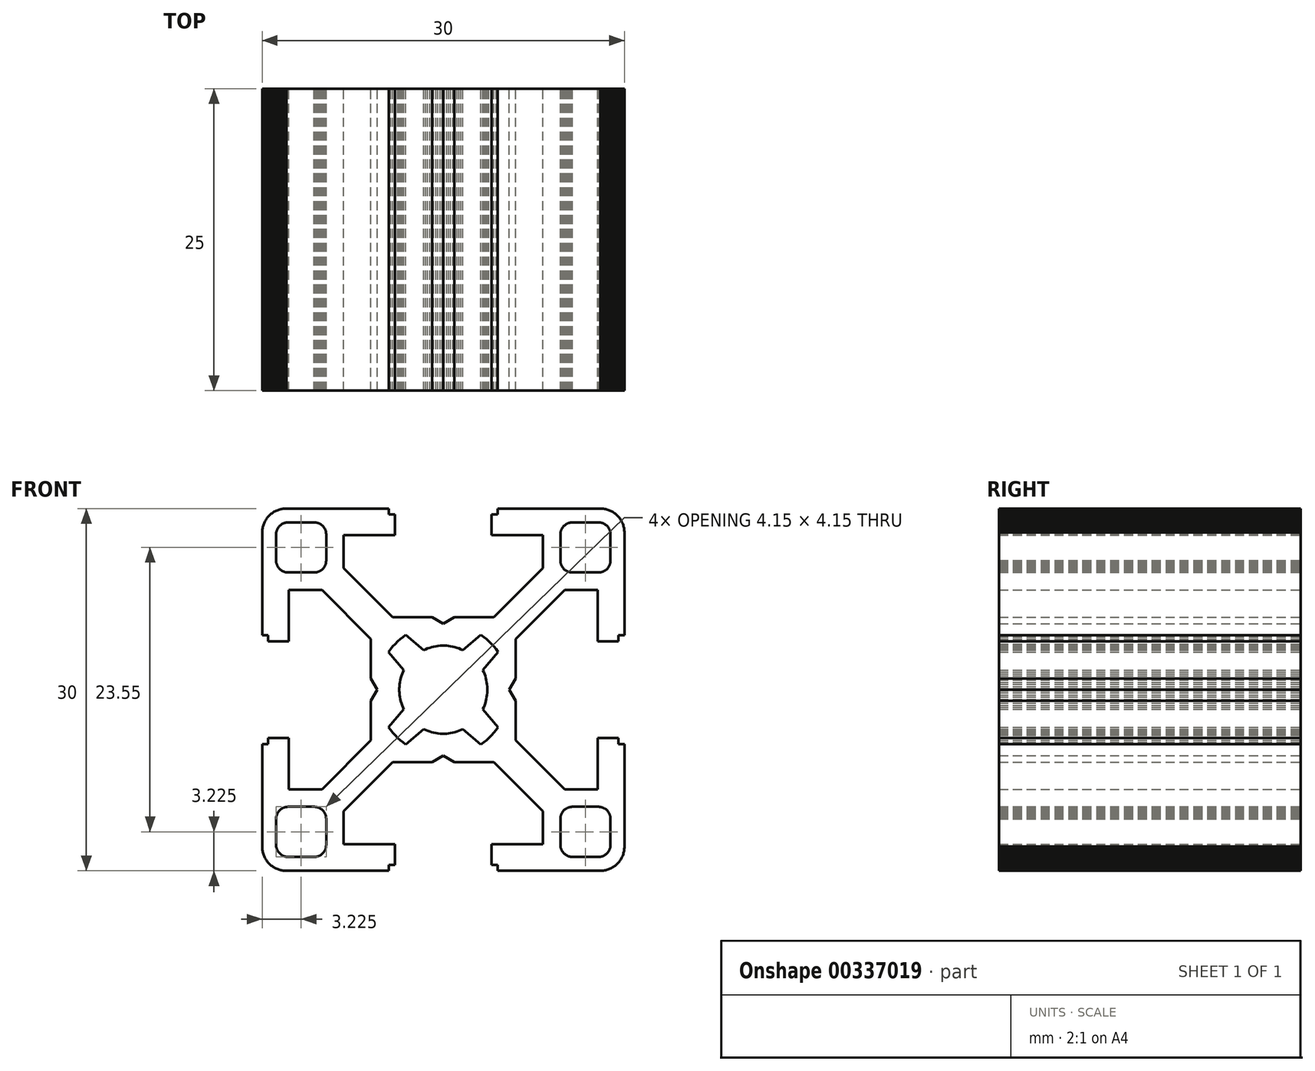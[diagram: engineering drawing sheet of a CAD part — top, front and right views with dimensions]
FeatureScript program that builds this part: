
annotation { "Feature Type Name" : "Feature", "Feature Type Description" : "" }
export const myFeature = defineFeature(function(context is Context, id is Id, definition is map)
    precondition{}
    {
        {
            var Q0;
            Q0=qCreatedBy(makeId("Front.planeOp"),FACE);
            var sketch = newSketch(context, id + "F0", { "sketchPlane" : qUnion([Q0])});
            skLineSegment(sketch, "E0", {"start": v(12.8, -8.25) * mm, "end": v(12.8, -4) * mm});
            skLineSegment(sketch, "E1", {"start": v(-12.8, 4) * mm, "end": v(-12.8, 8.25) * mm});
            skLineSegment(sketch, "E2", {"start": v(-13.85, -12.9) * mm, "end": v(-13.85, -12.85) * mm});
            skLineSegment(sketch, "E3", {"start": v(9.7, -12.9) * mm, "end": v(9.7, -12.85) * mm});
            skLineSegment(sketch, "E4", {"start": v(-9.7, -10.7) * mm, "end": v(-9.7, -10.66) * mm});
            skLineSegment(sketch, "E5", {"start": v(13.85, -10.7) * mm, "end": v(13.85, -10.66) * mm});
            skLineSegment(sketch, "E6", {"start": v(9.7, 10.66) * mm, "end": v(9.7, 10.7) * mm});
            skLineSegment(sketch, "E7", {"start": v(-13.85, 10.66) * mm, "end": v(-13.85, 10.7) * mm});
            skLineSegment(sketch, "E8", {"start": v(13.85, 12.85) * mm, "end": v(13.85, 12.9) * mm});
            skLineSegment(sketch, "E9", {"start": v(-9.7, 12.85) * mm, "end": v(-9.7, 12.9) * mm});
            skLineSegment(sketch, "E10", {"start": v(-15, -13.09) * mm, "end": v(-15, -13) * mm});
            skLineSegment(sketch, "E11", {"start": v(15, 13) * mm, "end": v(15, 13.09) * mm});
            skLineSegment(sketch, "E12", {"start": v(-3.64, -0.26) * mm, "end": v(-3.65, -0.09) * mm});
            skLineSegment(sketch, "E13", {"start": v(3.65, 0.09) * mm, "end": v(3.64, 0.26) * mm});
            skLineSegment(sketch, "E14", {"start": v(9.7, -12.94) * mm, "end": v(9.7, -12.9) * mm});
            skLineSegment(sketch, "E15", {"start": v(-9.7, -10.66) * mm, "end": v(-9.7, -10.61) * mm});
            skLineSegment(sketch, "E16", {"start": v(9.7, 10.61) * mm, "end": v(9.7, 10.66) * mm});
            skLineSegment(sketch, "E17", {"start": v(-9.7, 12.9) * mm, "end": v(-9.7, 12.94) * mm});
            skLineSegment(sketch, "E18", {"start": v(-15, -13.18) * mm, "end": v(-15, -13.09) * mm});
            skLineSegment(sketch, "E19", {"start": v(15, 13.09) * mm, "end": v(15, 13.18) * mm});
            skLineSegment(sketch, "E20", {"start": v(-13.85, -12.94) * mm, "end": v(-13.85, -12.9) * mm});
            skLineSegment(sketch, "E21", {"start": v(13.85, -10.66) * mm, "end": v(13.85, -10.61) * mm});
            skLineSegment(sketch, "E22", {"start": v(-13.85, 10.61) * mm, "end": v(-13.85, 10.66) * mm});
            skLineSegment(sketch, "E23", {"start": v(13.85, 12.9) * mm, "end": v(13.85, 12.94) * mm});
            skLineSegment(sketch, "E24", {"start": v(-3.62, -0.44) * mm, "end": v(-3.64, -0.26) * mm});
            skLineSegment(sketch, "E25", {"start": v(3.64, 0.26) * mm, "end": v(3.62, 0.44) * mm});
            skLineSegment(sketch, "E26", {"start": v(13.85, -10.61) * mm, "end": v(13.84, -10.57) * mm});
            skLineSegment(sketch, "E27", {"start": v(-13.84, 10.57) * mm, "end": v(-13.85, 10.61) * mm});
            skLineSegment(sketch, "E28", {"start": v(-13.84, -12.98) * mm, "end": v(-13.85, -12.94) * mm});
            skLineSegment(sketch, "E29", {"start": v(13.85, 12.94) * mm, "end": v(13.84, 12.98) * mm});
            skLineSegment(sketch, "E30", {"start": v(-14.98, -13.27) * mm, "end": v(-15, -13.18) * mm});
            skLineSegment(sketch, "E31", {"start": v(15, 13.18) * mm, "end": v(14.98, 13.27) * mm});
            skLineSegment(sketch, "E32", {"start": v(-9.7, -10.61) * mm, "end": v(-9.7, -10.57) * mm});
            skLineSegment(sketch, "E33", {"start": v(9.7, 10.57) * mm, "end": v(9.7, 10.61) * mm});
            skLineSegment(sketch, "E34", {"start": v(9.7, -12.98) * mm, "end": v(9.7, -12.94) * mm});
            skLineSegment(sketch, "E35", {"start": v(-9.7, 12.94) * mm, "end": v(-9.7, 12.98) * mm});
            skLineSegment(sketch, "E36", {"start": v(-3.6, -0.61) * mm, "end": v(-3.62, -0.44) * mm});
            skLineSegment(sketch, "E37", {"start": v(3.62, 0.44) * mm, "end": v(3.6, 0.61) * mm});
            skLineSegment(sketch, "E38", {"start": v(-13.83, -13.03) * mm, "end": v(-13.84, -12.98) * mm});
            skLineSegment(sketch, "E39", {"start": v(9.72, -13.03) * mm, "end": v(9.7, -12.98) * mm});
            skLineSegment(sketch, "E40", {"start": v(13.84, 12.98) * mm, "end": v(13.83, 13.03) * mm});
            skLineSegment(sketch, "E41", {"start": v(-9.7, 12.98) * mm, "end": v(-9.72, 13.03) * mm});
            skLineSegment(sketch, "E42", {"start": v(-14.97, -13.36) * mm, "end": v(-14.98, -13.27) * mm});
            skLineSegment(sketch, "E43", {"start": v(14.98, 13.27) * mm, "end": v(14.97, 13.36) * mm});
            skLineSegment(sketch, "E44", {"start": v(-9.7, -10.57) * mm, "end": v(-9.72, -10.52) * mm});
            skLineSegment(sketch, "E45", {"start": v(13.84, -10.57) * mm, "end": v(13.83, -10.52) * mm});
            skLineSegment(sketch, "E46", {"start": v(9.72, 10.52) * mm, "end": v(9.7, 10.57) * mm});
            skLineSegment(sketch, "E47", {"start": v(-13.83, 10.52) * mm, "end": v(-13.84, 10.57) * mm});
            skLineSegment(sketch, "E48", {"start": v(-3.56, -0.79) * mm, "end": v(-3.6, -0.61) * mm});
            skLineSegment(sketch, "E49", {"start": v(3.6, 0.61) * mm, "end": v(3.56, 0.79) * mm});
            skLineSegment(sketch, "E50", {"start": v(-14.95, -13.45) * mm, "end": v(-14.97, -13.36) * mm});
            skLineSegment(sketch, "E51", {"start": v(14.97, 13.36) * mm, "end": v(14.95, 13.45) * mm});
            skLineSegment(sketch, "E52", {"start": v(-13.82, -13.07) * mm, "end": v(-13.83, -13.03) * mm});
            skLineSegment(sketch, "E53", {"start": v(9.73, -13.07) * mm, "end": v(9.72, -13.03) * mm});
            skLineSegment(sketch, "E54", {"start": v(-9.72, -10.52) * mm, "end": v(-9.73, -10.48) * mm});
            skLineSegment(sketch, "E55", {"start": v(13.83, -10.52) * mm, "end": v(13.82, -10.48) * mm});
            skLineSegment(sketch, "E56", {"start": v(9.73, 10.48) * mm, "end": v(9.72, 10.52) * mm});
            skLineSegment(sketch, "E57", {"start": v(-13.82, 10.48) * mm, "end": v(-13.83, 10.52) * mm});
            skLineSegment(sketch, "E58", {"start": v(13.83, 13.03) * mm, "end": v(13.82, 13.07) * mm});
            skLineSegment(sketch, "E59", {"start": v(-9.72, 13.03) * mm, "end": v(-9.73, 13.07) * mm});
            skLineSegment(sketch, "E60", {"start": v(-3.52, -0.96) * mm, "end": v(-3.56, -0.79) * mm});
            skLineSegment(sketch, "E61", {"start": v(3.56, 0.79) * mm, "end": v(3.52, 0.96) * mm});
            skLineSegment(sketch, "E62", {"start": v(-14.93, -13.53) * mm, "end": v(-14.95, -13.45) * mm});
            skLineSegment(sketch, "E63", {"start": v(-9.73, -10.48) * mm, "end": v(-9.74, -10.43) * mm});
            skLineSegment(sketch, "E64", {"start": v(13.82, -10.48) * mm, "end": v(13.81, -10.43) * mm});
            skLineSegment(sketch, "E65", {"start": v(9.74, 10.43) * mm, "end": v(9.73, 10.48) * mm});
            skLineSegment(sketch, "E66", {"start": v(-13.81, 10.43) * mm, "end": v(-13.82, 10.48) * mm});
            skLineSegment(sketch, "E67", {"start": v(14.95, 13.45) * mm, "end": v(14.93, 13.53) * mm});
            skLineSegment(sketch, "E68", {"start": v(-13.81, -13.12) * mm, "end": v(-13.82, -13.07) * mm});
            skLineSegment(sketch, "E69", {"start": v(9.74, -13.12) * mm, "end": v(9.73, -13.07) * mm});
            skLineSegment(sketch, "E70", {"start": v(13.82, 13.07) * mm, "end": v(13.81, 13.12) * mm});
            skLineSegment(sketch, "E71", {"start": v(-9.73, 13.07) * mm, "end": v(-9.74, 13.12) * mm});
            skLineSegment(sketch, "E72", {"start": v(-3.47, -1.13) * mm, "end": v(-3.52, -0.96) * mm});
            skLineSegment(sketch, "E73", {"start": v(3.52, 0.96) * mm, "end": v(3.47, 1.13) * mm});
            skLineSegment(sketch, "E74", {"start": v(-13.8, -13.16) * mm, "end": v(-13.81, -13.12) * mm});
            skLineSegment(sketch, "E75", {"start": v(9.75, -13.16) * mm, "end": v(9.74, -13.12) * mm});
            skLineSegment(sketch, "E76", {"start": v(13.81, 13.12) * mm, "end": v(13.8, 13.16) * mm});
            skLineSegment(sketch, "E77", {"start": v(-9.74, 13.12) * mm, "end": v(-9.75, 13.16) * mm});
            skLineSegment(sketch, "E78", {"start": v(-9.74, -10.43) * mm, "end": v(-9.75, -10.4) * mm});
            skLineSegment(sketch, "E79", {"start": v(13.81, -10.43) * mm, "end": v(13.8, -10.4) * mm});
            skLineSegment(sketch, "E80", {"start": v(9.75, 10.4) * mm, "end": v(9.74, 10.43) * mm});
            skLineSegment(sketch, "E81", {"start": v(-13.8, 10.4) * mm, "end": v(-13.81, 10.43) * mm});
            skLineSegment(sketch, "E82", {"start": v(-14.9, -13.62) * mm, "end": v(-14.93, -13.53) * mm});
            skLineSegment(sketch, "E83", {"start": v(14.93, 13.53) * mm, "end": v(14.9, 13.62) * mm});
            skLineSegment(sketch, "E84", {"start": v(-14.87, -13.7) * mm, "end": v(-14.9, -13.62) * mm});
            skLineSegment(sketch, "E85", {"start": v(14.9, 13.62) * mm, "end": v(14.87, 13.7) * mm});
            skLineSegment(sketch, "E86", {"start": v(-13.79, -13.2) * mm, "end": v(-13.8, -13.16) * mm});
            skLineSegment(sketch, "E87", {"start": v(9.76, -13.2) * mm, "end": v(9.75, -13.16) * mm});
            skLineSegment(sketch, "E88", {"start": v(-9.75, -10.4) * mm, "end": v(-9.76, -10.35) * mm});
            skLineSegment(sketch, "E89", {"start": v(13.8, -10.4) * mm, "end": v(13.79, -10.35) * mm});
            skLineSegment(sketch, "E90", {"start": v(9.76, 10.35) * mm, "end": v(9.75, 10.4) * mm});
            skLineSegment(sketch, "E91", {"start": v(-13.79, 10.35) * mm, "end": v(-13.8, 10.4) * mm});
            skLineSegment(sketch, "E92", {"start": v(13.8, 13.16) * mm, "end": v(13.79, 13.2) * mm});
            skLineSegment(sketch, "E93", {"start": v(-9.75, 13.16) * mm, "end": v(-9.76, 13.2) * mm});
            skLineSegment(sketch, "E94", {"start": v(-3.41, -1.3) * mm, "end": v(-3.47, -1.13) * mm});
            skLineSegment(sketch, "E95", {"start": v(3.47, 1.13) * mm, "end": v(3.41, 1.3) * mm});
            skLineSegment(sketch, "E96", {"start": v(-14.84, -13.79) * mm, "end": v(-14.87, -13.7) * mm});
            skLineSegment(sketch, "E97", {"start": v(14.87, 13.7) * mm, "end": v(14.84, 13.79) * mm});
            skLineSegment(sketch, "E98", {"start": v(9.78, -13.24) * mm, "end": v(9.76, -13.2) * mm});
            skLineSegment(sketch, "E99", {"start": v(-9.76, -10.35) * mm, "end": v(-9.78, -10.3) * mm});
            skLineSegment(sketch, "E100", {"start": v(9.78, 10.3) * mm, "end": v(9.76, 10.35) * mm});
            skLineSegment(sketch, "E101", {"start": v(-9.76, 13.2) * mm, "end": v(-9.78, 13.24) * mm});
            skLineSegment(sketch, "E102", {"start": v(-13.77, -13.24) * mm, "end": v(-13.79, -13.2) * mm});
            skLineSegment(sketch, "E103", {"start": v(13.79, -10.35) * mm, "end": v(13.77, -10.3) * mm});
            skLineSegment(sketch, "E104", {"start": v(-13.77, 10.3) * mm, "end": v(-13.79, 10.35) * mm});
            skLineSegment(sketch, "E105", {"start": v(13.79, 13.2) * mm, "end": v(13.77, 13.24) * mm});
            skLineSegment(sketch, "E106", {"start": v(-3.35, -1.46) * mm, "end": v(-3.41, -1.3) * mm});
            skLineSegment(sketch, "E107", {"start": v(3.41, 1.3) * mm, "end": v(3.35, 1.46) * mm});
            skLineSegment(sketch, "E108", {"start": v(-13.75, -13.28) * mm, "end": v(-13.77, -13.24) * mm});
            skLineSegment(sketch, "E109", {"start": v(13.77, -10.3) * mm, "end": v(13.75, -10.27) * mm});
            skLineSegment(sketch, "E110", {"start": v(-13.75, 10.27) * mm, "end": v(-13.77, 10.3) * mm});
            skLineSegment(sketch, "E111", {"start": v(13.77, 13.24) * mm, "end": v(13.75, 13.28) * mm});
            skLineSegment(sketch, "E112", {"start": v(9.8, -13.28) * mm, "end": v(9.78, -13.24) * mm});
            skLineSegment(sketch, "E113", {"start": v(-9.78, -10.3) * mm, "end": v(-9.8, -10.27) * mm});
            skLineSegment(sketch, "E114", {"start": v(9.8, 10.27) * mm, "end": v(9.78, 10.3) * mm});
            skLineSegment(sketch, "E115", {"start": v(-9.78, 13.24) * mm, "end": v(-9.8, 13.28) * mm});
            skLineSegment(sketch, "E116", {"start": v(-14.8, -13.87) * mm, "end": v(-14.84, -13.79) * mm});
            skLineSegment(sketch, "E117", {"start": v(14.84, 13.79) * mm, "end": v(14.8, 13.87) * mm});
            skLineSegment(sketch, "E118", {"start": v(-3.27, -1.62) * mm, "end": v(-3.35, -1.46) * mm});
            skLineSegment(sketch, "E119", {"start": v(3.35, 1.46) * mm, "end": v(3.27, 1.62) * mm});
            skLineSegment(sketch, "E120", {"start": v(-13.73, -13.32) * mm, "end": v(-13.75, -13.28) * mm});
            skLineSegment(sketch, "E121", {"start": v(13.75, -10.27) * mm, "end": v(13.73, -10.23) * mm});
            skLineSegment(sketch, "E122", {"start": v(-13.73, 10.23) * mm, "end": v(-13.75, 10.27) * mm});
            skLineSegment(sketch, "E123", {"start": v(13.75, 13.28) * mm, "end": v(13.73, 13.32) * mm});
            skLineSegment(sketch, "E124", {"start": v(-14.76, -13.95) * mm, "end": v(-14.8, -13.87) * mm});
            skLineSegment(sketch, "E125", {"start": v(14.8, 13.87) * mm, "end": v(14.76, 13.95) * mm});
            skLineSegment(sketch, "E126", {"start": v(9.82, -13.32) * mm, "end": v(9.8, -13.28) * mm});
            skLineSegment(sketch, "E127", {"start": v(-9.8, -10.27) * mm, "end": v(-9.82, -10.23) * mm});
            skLineSegment(sketch, "E128", {"start": v(9.82, 10.23) * mm, "end": v(9.8, 10.27) * mm});
            skLineSegment(sketch, "E129", {"start": v(-9.8, 13.28) * mm, "end": v(-9.82, 13.32) * mm});
            skLineSegment(sketch, "E130", {"start": v(-9.82, -10.23) * mm, "end": v(-9.84, -10.19) * mm});
            skLineSegment(sketch, "E131", {"start": v(9.84, 10.19) * mm, "end": v(9.82, 10.23) * mm});
            skLineSegment(sketch, "E132", {"start": v(9.84, -13.36) * mm, "end": v(9.82, -13.32) * mm});
            skLineSegment(sketch, "E133", {"start": v(-9.82, 13.32) * mm, "end": v(-9.84, 13.36) * mm});
            skLineSegment(sketch, "E134", {"start": v(-14.72, -14.03) * mm, "end": v(-14.76, -13.95) * mm});
            skLineSegment(sketch, "E135", {"start": v(14.76, 13.95) * mm, "end": v(14.72, 14.03) * mm});
            skLineSegment(sketch, "E136", {"start": v(13.73, -10.23) * mm, "end": v(13.7, -10.19) * mm});
            skLineSegment(sketch, "E137", {"start": v(-13.7, 10.19) * mm, "end": v(-13.73, 10.23) * mm});
            skLineSegment(sketch, "E138", {"start": v(-13.7, -13.36) * mm, "end": v(-13.73, -13.32) * mm});
            skLineSegment(sketch, "E139", {"start": v(13.73, 13.32) * mm, "end": v(13.7, 13.36) * mm});
            skLineSegment(sketch, "E140", {"start": v(6, -0.92) * mm, "end": v(5.47, 0) * mm});
            skLineSegment(sketch, "E141", {"start": v(-5.47, 0) * mm, "end": v(-6, 0.92) * mm});
            skLineSegment(sketch, "E142", {"start": v(-13.68, -13.4) * mm, "end": v(-13.7, -13.36) * mm});
            skLineSegment(sketch, "E143", {"start": v(13.7, 13.36) * mm, "end": v(13.68, 13.4) * mm});
            skLineSegment(sketch, "E144", {"start": v(13.7, -10.19) * mm, "end": v(13.68, -10.15) * mm});
            skLineSegment(sketch, "E145", {"start": v(-13.68, 10.15) * mm, "end": v(-13.7, 10.19) * mm});
            skLineSegment(sketch, "E146", {"start": v(-14.67, -14.1) * mm, "end": v(-14.72, -14.03) * mm});
            skLineSegment(sketch, "E147", {"start": v(14.72, 14.03) * mm, "end": v(14.67, 14.1) * mm});
            skLineSegment(sketch, "E148", {"start": v(9.87, -13.4) * mm, "end": v(9.84, -13.36) * mm});
            skLineSegment(sketch, "E149", {"start": v(-9.84, 13.36) * mm, "end": v(-9.87, 13.4) * mm});
            skLineSegment(sketch, "E150", {"start": v(-9.84, -10.19) * mm, "end": v(-9.87, -10.15) * mm});
            skLineSegment(sketch, "E151", {"start": v(9.87, 10.15) * mm, "end": v(9.84, 10.19) * mm});
            skLineSegment(sketch, "E152", {"start": v(-13.66, -13.44) * mm, "end": v(-13.68, -13.4) * mm});
            skLineSegment(sketch, "E153", {"start": v(9.9, -13.44) * mm, "end": v(9.87, -13.4) * mm});
            skLineSegment(sketch, "E154", {"start": v(-9.87, -10.15) * mm, "end": v(-9.9, -10.11) * mm});
            skLineSegment(sketch, "E155", {"start": v(13.68, -10.15) * mm, "end": v(13.66, -10.11) * mm});
            skLineSegment(sketch, "E156", {"start": v(9.9, 10.11) * mm, "end": v(9.87, 10.15) * mm});
            skLineSegment(sketch, "E157", {"start": v(-13.66, 10.11) * mm, "end": v(-13.68, 10.15) * mm});
            skLineSegment(sketch, "E158", {"start": v(13.68, 13.4) * mm, "end": v(13.66, 13.44) * mm});
            skLineSegment(sketch, "E159", {"start": v(-9.87, 13.4) * mm, "end": v(-9.9, 13.44) * mm});
            skLineSegment(sketch, "E160", {"start": v(-14.62, -14.18) * mm, "end": v(-14.67, -14.1) * mm});
            skLineSegment(sketch, "E161", {"start": v(14.67, 14.1) * mm, "end": v(14.62, 14.18) * mm});
            skLineSegment(sketch, "E162", {"start": v(-4.36, -3.35) * mm, "end": v(-4.53, -3.12) * mm});
            skLineSegment(sketch, "E163", {"start": v(4.53, 3.12) * mm, "end": v(4.36, 3.35) * mm});
            skLineSegment(sketch, "E164", {"start": v(9.92, -13.47) * mm, "end": v(9.9, -13.44) * mm});
            skLineSegment(sketch, "E165", {"start": v(-9.9, -10.11) * mm, "end": v(-9.92, -10.08) * mm});
            skLineSegment(sketch, "E166", {"start": v(9.92, 10.08) * mm, "end": v(9.9, 10.11) * mm});
            skLineSegment(sketch, "E167", {"start": v(-9.9, 13.44) * mm, "end": v(-9.92, 13.47) * mm});
            skLineSegment(sketch, "E168", {"start": v(-14.56, -14.25) * mm, "end": v(-14.62, -14.18) * mm});
            skLineSegment(sketch, "E169", {"start": v(14.62, 14.18) * mm, "end": v(14.56, 14.25) * mm});
            skLineSegment(sketch, "E170", {"start": v(-13.63, -13.47) * mm, "end": v(-13.66, -13.44) * mm});
            skLineSegment(sketch, "E171", {"start": v(13.66, -10.11) * mm, "end": v(13.63, -10.08) * mm});
            skLineSegment(sketch, "E172", {"start": v(-13.63, 10.08) * mm, "end": v(-13.66, 10.11) * mm});
            skLineSegment(sketch, "E173", {"start": v(13.66, 13.44) * mm, "end": v(13.63, 13.47) * mm});
            skLineSegment(sketch, "E174", {"start": v(-4.18, -3.57) * mm, "end": v(-4.36, -3.35) * mm});
            skLineSegment(sketch, "E175", {"start": v(4.36, 3.35) * mm, "end": v(4.18, 3.57) * mm});
            skLineSegment(sketch, "E176", {"start": v(-14.5, -14.32) * mm, "end": v(-14.56, -14.25) * mm});
            skLineSegment(sketch, "E177", {"start": v(13.63, -10.08) * mm, "end": v(13.6, -10.04) * mm});
            skLineSegment(sketch, "E178", {"start": v(-13.6, 10.04) * mm, "end": v(-13.63, 10.08) * mm});
            skLineSegment(sketch, "E179", {"start": v(14.56, 14.25) * mm, "end": v(14.5, 14.32) * mm});
            skLineSegment(sketch, "E180", {"start": v(-13.6, -13.5) * mm, "end": v(-13.63, -13.47) * mm});
            skLineSegment(sketch, "E181", {"start": v(13.63, 13.47) * mm, "end": v(13.6, 13.5) * mm});
            skLineSegment(sketch, "E182", {"start": v(-9.92, -10.08) * mm, "end": v(-9.95, -10.04) * mm});
            skLineSegment(sketch, "E183", {"start": v(9.95, 10.04) * mm, "end": v(9.92, 10.08) * mm});
            skLineSegment(sketch, "E184", {"start": v(9.95, -13.5) * mm, "end": v(9.92, -13.47) * mm});
            skLineSegment(sketch, "E185", {"start": v(-9.92, 13.47) * mm, "end": v(-9.95, 13.5) * mm});
            skLineSegment(sketch, "E186", {"start": v(4.53, -3.12) * mm, "end": v(3.27, -1.62) * mm});
            skLineSegment(sketch, "E187", {"start": v(-3.27, 1.62) * mm, "end": v(-4.53, 3.12) * mm});
            skLineSegment(sketch, "E188", {"start": v(-3.99, -3.79) * mm, "end": v(-4.18, -3.57) * mm});
            skLineSegment(sketch, "E189", {"start": v(4.18, 3.57) * mm, "end": v(3.99, 3.79) * mm});
            skLineSegment(sketch, "E190", {"start": v(-13.57, -13.54) * mm, "end": v(-13.6, -13.5) * mm});
            skLineSegment(sketch, "E191", {"start": v(9.98, -13.54) * mm, "end": v(9.95, -13.5) * mm});
            skLineSegment(sketch, "E192", {"start": v(-9.95, -10.04) * mm, "end": v(-9.98, -10) * mm});
            skLineSegment(sketch, "E193", {"start": v(13.6, -10.04) * mm, "end": v(13.57, -10) * mm});
            skLineSegment(sketch, "E194", {"start": v(9.98, 10) * mm, "end": v(9.95, 10.04) * mm});
            skLineSegment(sketch, "E195", {"start": v(-13.57, 10) * mm, "end": v(-13.6, 10.04) * mm});
            skLineSegment(sketch, "E196", {"start": v(13.6, 13.5) * mm, "end": v(13.57, 13.54) * mm});
            skLineSegment(sketch, "E197", {"start": v(-9.95, 13.5) * mm, "end": v(-9.98, 13.54) * mm});
            skLineSegment(sketch, "E198", {"start": v(-14.45, -14.38) * mm, "end": v(-14.5, -14.32) * mm});
            skLineSegment(sketch, "E199", {"start": v(14.5, 14.32) * mm, "end": v(14.45, 14.38) * mm});
            skLineSegment(sketch, "E200", {"start": v(10, -13.57) * mm, "end": v(9.98, -13.54) * mm});
            skLineSegment(sketch, "E201", {"start": v(-9.98, 13.54) * mm, "end": v(-10, 13.57) * mm});
            skLineSegment(sketch, "E202", {"start": v(-14.38, -14.45) * mm, "end": v(-14.45, -14.38) * mm});
            skLineSegment(sketch, "E203", {"start": v(-13.54, -13.57) * mm, "end": v(-13.57, -13.54) * mm});
            skLineSegment(sketch, "E204", {"start": v(8.25, -10.05) * mm, "end": v(4.2, -6) * mm});
            skLineSegment(sketch, "E205", {"start": v(-9.98, -10) * mm, "end": v(-10, -9.98) * mm});
            skLineSegment(sketch, "E206", {"start": v(10.05, -8.25) * mm, "end": v(6, -4.2) * mm});
            skLineSegment(sketch, "E207", {"start": v(-3.79, -3.99) * mm, "end": v(-3.99, -3.79) * mm});
            skLineSegment(sketch, "E208", {"start": v(3.99, 3.79) * mm, "end": v(3.79, 3.99) * mm});
            skLineSegment(sketch, "E209", {"start": v(-6, 4.2) * mm, "end": v(-10.05, 8.25) * mm});
            skLineSegment(sketch, "E210", {"start": v(-4.2, 6) * mm, "end": v(-8.25, 10.05) * mm});
            skLineSegment(sketch, "E211", {"start": v(10, 9.98) * mm, "end": v(9.98, 10) * mm});
            skLineSegment(sketch, "E212", {"start": v(13.57, 13.54) * mm, "end": v(13.54, 13.57) * mm});
            skLineSegment(sketch, "E213", {"start": v(14.45, 14.38) * mm, "end": v(14.38, 14.45) * mm});
            skLineSegment(sketch, "E214", {"start": v(13.57, -10) * mm, "end": v(13.54, -9.98) * mm});
            skLineSegment(sketch, "E215", {"start": v(-13.54, 9.98) * mm, "end": v(-13.57, 10) * mm});
            skLineSegment(sketch, "E216", {"start": v(-14.32, -14.5) * mm, "end": v(-14.38, -14.45) * mm});
            skLineSegment(sketch, "E217", {"start": v(14.38, 14.45) * mm, "end": v(14.32, 14.5) * mm});
            skLineSegment(sketch, "E218", {"start": v(-13.5, -13.6) * mm, "end": v(-13.54, -13.57) * mm});
            skLineSegment(sketch, "E219", {"start": v(10.04, -13.6) * mm, "end": v(10, -13.57) * mm});
            skLineSegment(sketch, "E220", {"start": v(-10, -9.98) * mm, "end": v(-10.04, -9.95) * mm});
            skLineSegment(sketch, "E221", {"start": v(13.54, -9.98) * mm, "end": v(13.5, -9.95) * mm});
            skLineSegment(sketch, "E222", {"start": v(10.04, 9.95) * mm, "end": v(10, 9.98) * mm});
            skLineSegment(sketch, "E223", {"start": v(-13.5, 9.95) * mm, "end": v(-13.54, 9.98) * mm});
            skLineSegment(sketch, "E224", {"start": v(13.54, 13.57) * mm, "end": v(13.5, 13.6) * mm});
            skLineSegment(sketch, "E225", {"start": v(-10, 13.57) * mm, "end": v(-10.04, 13.6) * mm});
            skLineSegment(sketch, "E226", {"start": v(-3.57, -4.18) * mm, "end": v(-3.79, -3.99) * mm});
            skLineSegment(sketch, "E227", {"start": v(3.79, 3.99) * mm, "end": v(3.57, 4.18) * mm});
            skLineSegment(sketch, "E228", {"start": v(3.12, -4.53) * mm, "end": v(1.62, -3.27) * mm});
            skLineSegment(sketch, "E229", {"start": v(-1.62, 3.27) * mm, "end": v(-3.12, 4.53) * mm});
            skLineSegment(sketch, "E230", {"start": v(13.5, -9.95) * mm, "end": v(13.47, -9.92) * mm});
            skLineSegment(sketch, "E231", {"start": v(-13.47, 9.92) * mm, "end": v(-13.5, 9.95) * mm});
            skLineSegment(sketch, "E232", {"start": v(-10.04, -9.95) * mm, "end": v(-10.08, -9.92) * mm});
            skLineSegment(sketch, "E233", {"start": v(10.08, 9.92) * mm, "end": v(10.04, 9.95) * mm});
            skLineSegment(sketch, "E234", {"start": v(-13.47, -13.63) * mm, "end": v(-13.5, -13.6) * mm});
            skLineSegment(sketch, "E235", {"start": v(13.5, 13.6) * mm, "end": v(13.47, 13.63) * mm});
            skLineSegment(sketch, "E236", {"start": v(-14.25, -14.56) * mm, "end": v(-14.32, -14.5) * mm});
            skLineSegment(sketch, "E237", {"start": v(10.08, -13.63) * mm, "end": v(10.04, -13.6) * mm});
            skLineSegment(sketch, "E238", {"start": v(-10.04, 13.6) * mm, "end": v(-10.08, 13.63) * mm});
            skLineSegment(sketch, "E239", {"start": v(14.32, 14.5) * mm, "end": v(14.25, 14.56) * mm});
            skLineSegment(sketch, "E240", {"start": v(-3.35, -4.36) * mm, "end": v(-3.57, -4.18) * mm});
            skLineSegment(sketch, "E241", {"start": v(3.57, 4.18) * mm, "end": v(3.35, 4.36) * mm});
            skLineSegment(sketch, "E242", {"start": v(-13.44, -13.66) * mm, "end": v(-13.47, -13.63) * mm});
            skLineSegment(sketch, "E243", {"start": v(10.11, -13.66) * mm, "end": v(10.08, -13.63) * mm});
            skLineSegment(sketch, "E244", {"start": v(13.47, 13.63) * mm, "end": v(13.44, 13.66) * mm});
            skLineSegment(sketch, "E245", {"start": v(-10.08, 13.63) * mm, "end": v(-10.11, 13.66) * mm});
            skLineSegment(sketch, "E246", {"start": v(-14.18, -14.62) * mm, "end": v(-14.25, -14.56) * mm});
            skLineSegment(sketch, "E247", {"start": v(14.25, 14.56) * mm, "end": v(14.18, 14.62) * mm});
            skLineSegment(sketch, "E248", {"start": v(-10.08, -9.92) * mm, "end": v(-10.11, -9.9) * mm});
            skLineSegment(sketch, "E249", {"start": v(13.47, -9.92) * mm, "end": v(13.44, -9.9) * mm});
            skLineSegment(sketch, "E250", {"start": v(10.11, 9.9) * mm, "end": v(10.08, 9.92) * mm});
            skLineSegment(sketch, "E251", {"start": v(-13.44, 9.9) * mm, "end": v(-13.47, 9.92) * mm});
            skLineSegment(sketch, "E252", {"start": v(-3.12, -4.53) * mm, "end": v(-3.35, -4.36) * mm});
            skLineSegment(sketch, "E253", {"start": v(3.35, 4.36) * mm, "end": v(3.12, 4.53) * mm});
            skLineSegment(sketch, "E254", {"start": v(-14.1, -14.67) * mm, "end": v(-14.18, -14.62) * mm});
            skLineSegment(sketch, "E255", {"start": v(14.18, 14.62) * mm, "end": v(14.1, 14.67) * mm});
            skLineSegment(sketch, "E256", {"start": v(-13.4, -13.68) * mm, "end": v(-13.44, -13.66) * mm});
            skLineSegment(sketch, "E257", {"start": v(10.15, -13.68) * mm, "end": v(10.11, -13.66) * mm});
            skLineSegment(sketch, "E258", {"start": v(-10.11, -9.9) * mm, "end": v(-10.15, -9.87) * mm});
            skLineSegment(sketch, "E259", {"start": v(13.44, -9.9) * mm, "end": v(13.4, -9.87) * mm});
            skLineSegment(sketch, "E260", {"start": v(10.15, 9.87) * mm, "end": v(10.11, 9.9) * mm});
            skLineSegment(sketch, "E261", {"start": v(-13.4, 9.87) * mm, "end": v(-13.44, 9.9) * mm});
            skLineSegment(sketch, "E262", {"start": v(13.44, 13.66) * mm, "end": v(13.4, 13.68) * mm});
            skLineSegment(sketch, "E263", {"start": v(-10.11, 13.66) * mm, "end": v(-10.15, 13.68) * mm});
            skLineSegment(sketch, "E264", {"start": v(-10.15, -9.87) * mm, "end": v(-10.19, -9.84) * mm});
            skLineSegment(sketch, "E265", {"start": v(10.19, 9.84) * mm, "end": v(10.15, 9.87) * mm});
            skLineSegment(sketch, "E266", {"start": v(13.4, -9.87) * mm, "end": v(13.36, -9.84) * mm});
            skLineSegment(sketch, "E267", {"start": v(-13.36, 9.84) * mm, "end": v(-13.4, 9.87) * mm});
            skLineSegment(sketch, "E268", {"start": v(-14.03, -14.72) * mm, "end": v(-14.1, -14.67) * mm});
            skLineSegment(sketch, "E269", {"start": v(14.1, 14.67) * mm, "end": v(14.03, 14.72) * mm});
            skLineSegment(sketch, "E270", {"start": v(10.19, -13.7) * mm, "end": v(10.15, -13.68) * mm});
            skLineSegment(sketch, "E271", {"start": v(-10.15, 13.68) * mm, "end": v(-10.19, 13.7) * mm});
            skLineSegment(sketch, "E272", {"start": v(-13.36, -13.7) * mm, "end": v(-13.4, -13.68) * mm});
            skLineSegment(sketch, "E273", {"start": v(13.4, 13.68) * mm, "end": v(13.36, 13.7) * mm});
            skLineSegment(sketch, "E274", {"start": v(0.92, -6) * mm, "end": v(0, -5.47) * mm});
            skLineSegment(sketch, "E275", {"start": v(0, 5.47) * mm, "end": v(-0.92, 6) * mm});
            skLineSegment(sketch, "E276", {"start": v(-13.32, -13.73) * mm, "end": v(-13.36, -13.7) * mm});
            skLineSegment(sketch, "E277", {"start": v(13.36, 13.7) * mm, "end": v(13.32, 13.73) * mm});
            skLineSegment(sketch, "E278", {"start": v(10.23, -13.73) * mm, "end": v(10.19, -13.7) * mm});
            skLineSegment(sketch, "E279", {"start": v(-10.19, 13.7) * mm, "end": v(-10.23, 13.73) * mm});
            skLineSegment(sketch, "E280", {"start": v(-13.95, -14.76) * mm, "end": v(-14.03, -14.72) * mm});
            skLineSegment(sketch, "E281", {"start": v(14.03, 14.72) * mm, "end": v(13.95, 14.76) * mm});
            skLineSegment(sketch, "E282", {"start": v(13.36, -9.84) * mm, "end": v(13.32, -9.82) * mm});
            skLineSegment(sketch, "E283", {"start": v(-13.32, 9.82) * mm, "end": v(-13.36, 9.84) * mm});
            skLineSegment(sketch, "E284", {"start": v(-10.19, -9.84) * mm, "end": v(-10.23, -9.82) * mm});
            skLineSegment(sketch, "E285", {"start": v(10.23, 9.82) * mm, "end": v(10.19, 9.84) * mm});
            skLineSegment(sketch, "E286", {"start": v(-10.23, -9.82) * mm, "end": v(-10.27, -9.8) * mm});
            skLineSegment(sketch, "E287", {"start": v(13.32, -9.82) * mm, "end": v(13.28, -9.8) * mm});
            skLineSegment(sketch, "E288", {"start": v(10.27, 9.8) * mm, "end": v(10.23, 9.82) * mm});
            skLineSegment(sketch, "E289", {"start": v(-13.28, 9.8) * mm, "end": v(-13.32, 9.82) * mm});
            skLineSegment(sketch, "E290", {"start": v(-13.87, -14.8) * mm, "end": v(-13.95, -14.76) * mm});
            skLineSegment(sketch, "E291", {"start": v(13.95, 14.76) * mm, "end": v(13.87, 14.8) * mm});
            skLineSegment(sketch, "E292", {"start": v(-13.28, -13.75) * mm, "end": v(-13.32, -13.73) * mm});
            skLineSegment(sketch, "E293", {"start": v(10.27, -13.75) * mm, "end": v(10.23, -13.73) * mm});
            skLineSegment(sketch, "E294", {"start": v(13.32, 13.73) * mm, "end": v(13.28, 13.75) * mm});
            skLineSegment(sketch, "E295", {"start": v(-10.23, 13.73) * mm, "end": v(-10.27, 13.75) * mm});
            skLineSegment(sketch, "E296", {"start": v(-1.46, -3.35) * mm, "end": v(-1.62, -3.27) * mm});
            skLineSegment(sketch, "E297", {"start": v(1.62, 3.27) * mm, "end": v(1.46, 3.35) * mm});
            skLineSegment(sketch, "E298", {"start": v(-13.79, -14.84) * mm, "end": v(-13.87, -14.8) * mm});
            skLineSegment(sketch, "E299", {"start": v(13.87, 14.8) * mm, "end": v(13.79, 14.84) * mm});
            skLineSegment(sketch, "E300", {"start": v(-10.27, -9.8) * mm, "end": v(-10.3, -9.78) * mm});
            skLineSegment(sketch, "E301", {"start": v(13.28, -9.8) * mm, "end": v(13.24, -9.78) * mm});
            skLineSegment(sketch, "E302", {"start": v(10.3, 9.78) * mm, "end": v(10.27, 9.8) * mm});
            skLineSegment(sketch, "E303", {"start": v(-13.24, 9.78) * mm, "end": v(-13.28, 9.8) * mm});
            skLineSegment(sketch, "E304", {"start": v(-13.24, -13.77) * mm, "end": v(-13.28, -13.75) * mm});
            skLineSegment(sketch, "E305", {"start": v(10.3, -13.77) * mm, "end": v(10.27, -13.75) * mm});
            skLineSegment(sketch, "E306", {"start": v(13.28, 13.75) * mm, "end": v(13.24, 13.77) * mm});
            skLineSegment(sketch, "E307", {"start": v(-10.27, 13.75) * mm, "end": v(-10.3, 13.77) * mm});
            skLineSegment(sketch, "E308", {"start": v(-1.3, -3.41) * mm, "end": v(-1.46, -3.35) * mm});
            skLineSegment(sketch, "E309", {"start": v(1.46, 3.35) * mm, "end": v(1.3, 3.41) * mm});
            skLineSegment(sketch, "E310", {"start": v(-13.2, -13.79) * mm, "end": v(-13.24, -13.77) * mm});
            skLineSegment(sketch, "E311", {"start": v(10.35, -13.79) * mm, "end": v(10.3, -13.77) * mm});
            skLineSegment(sketch, "E312", {"start": v(13.24, 13.77) * mm, "end": v(13.2, 13.79) * mm});
            skLineSegment(sketch, "E313", {"start": v(-10.3, 13.77) * mm, "end": v(-10.35, 13.79) * mm});
            skLineSegment(sketch, "E314", {"start": v(-10.3, -9.78) * mm, "end": v(-10.35, -9.76) * mm});
            skLineSegment(sketch, "E315", {"start": v(13.24, -9.78) * mm, "end": v(13.2, -9.76) * mm});
            skLineSegment(sketch, "E316", {"start": v(10.35, 9.76) * mm, "end": v(10.3, 9.78) * mm});
            skLineSegment(sketch, "E317", {"start": v(-13.2, 9.76) * mm, "end": v(-13.24, 9.78) * mm});
            skLineSegment(sketch, "E318", {"start": v(-13.7, -14.87) * mm, "end": v(-13.79, -14.84) * mm});
            skLineSegment(sketch, "E319", {"start": v(13.79, 14.84) * mm, "end": v(13.7, 14.87) * mm});
            skLineSegment(sketch, "E320", {"start": v(-1.13, -3.47) * mm, "end": v(-1.3, -3.41) * mm});
            skLineSegment(sketch, "E321", {"start": v(1.3, 3.41) * mm, "end": v(1.13, 3.47) * mm});
            skLineSegment(sketch, "E322", {"start": v(-13.16, -13.8) * mm, "end": v(-13.2, -13.79) * mm});
            skLineSegment(sketch, "E323", {"start": v(10.4, -13.8) * mm, "end": v(10.35, -13.79) * mm});
            skLineSegment(sketch, "E324", {"start": v(-10.35, -9.76) * mm, "end": v(-10.4, -9.75) * mm});
            skLineSegment(sketch, "E325", {"start": v(13.2, -9.76) * mm, "end": v(13.16, -9.75) * mm});
            skLineSegment(sketch, "E326", {"start": v(10.4, 9.75) * mm, "end": v(10.35, 9.76) * mm});
            skLineSegment(sketch, "E327", {"start": v(-13.16, 9.75) * mm, "end": v(-13.2, 9.76) * mm});
            skLineSegment(sketch, "E328", {"start": v(13.2, 13.79) * mm, "end": v(13.16, 13.8) * mm});
            skLineSegment(sketch, "E329", {"start": v(-10.35, 13.79) * mm, "end": v(-10.4, 13.8) * mm});
            skLineSegment(sketch, "E330", {"start": v(-13.62, -14.9) * mm, "end": v(-13.7, -14.87) * mm});
            skLineSegment(sketch, "E331", {"start": v(13.7, 14.87) * mm, "end": v(13.62, 14.9) * mm});
            skLineSegment(sketch, "E332", {"start": v(-13.53, -14.93) * mm, "end": v(-13.62, -14.9) * mm});
            skLineSegment(sketch, "E333", {"start": v(13.62, 14.9) * mm, "end": v(13.53, 14.93) * mm});
            skLineSegment(sketch, "E334", {"start": v(10.43, -13.81) * mm, "end": v(10.4, -13.8) * mm});
            skLineSegment(sketch, "E335", {"start": v(-10.4, -9.75) * mm, "end": v(-10.43, -9.74) * mm});
            skLineSegment(sketch, "E336", {"start": v(10.43, 9.74) * mm, "end": v(10.4, 9.75) * mm});
            skLineSegment(sketch, "E337", {"start": v(-10.4, 13.8) * mm, "end": v(-10.43, 13.81) * mm});
            skLineSegment(sketch, "E338", {"start": v(-13.12, -13.81) * mm, "end": v(-13.16, -13.8) * mm});
            skLineSegment(sketch, "E339", {"start": v(13.16, -9.75) * mm, "end": v(13.12, -9.74) * mm});
            skLineSegment(sketch, "E340", {"start": v(-13.12, 9.74) * mm, "end": v(-13.16, 9.75) * mm});
            skLineSegment(sketch, "E341", {"start": v(13.16, 13.8) * mm, "end": v(13.12, 13.81) * mm});
            skLineSegment(sketch, "E342", {"start": v(-0.96, -3.52) * mm, "end": v(-1.13, -3.47) * mm});
            skLineSegment(sketch, "E343", {"start": v(1.13, 3.47) * mm, "end": v(0.96, 3.52) * mm});
            skLineSegment(sketch, "E344", {"start": v(-13.07, -13.82) * mm, "end": v(-13.12, -13.81) * mm});
            skLineSegment(sketch, "E345", {"start": v(13.12, -9.74) * mm, "end": v(13.07, -9.73) * mm});
            skLineSegment(sketch, "E346", {"start": v(-13.07, 9.73) * mm, "end": v(-13.12, 9.74) * mm});
            skLineSegment(sketch, "E347", {"start": v(13.12, 13.81) * mm, "end": v(13.07, 13.82) * mm});
            skLineSegment(sketch, "E348", {"start": v(-13.45, -14.95) * mm, "end": v(-13.53, -14.93) * mm});
            skLineSegment(sketch, "E349", {"start": v(10.48, -13.82) * mm, "end": v(10.43, -13.81) * mm});
            skLineSegment(sketch, "E350", {"start": v(-10.43, -9.74) * mm, "end": v(-10.48, -9.73) * mm});
            skLineSegment(sketch, "E351", {"start": v(10.48, 9.73) * mm, "end": v(10.43, 9.74) * mm});
            skLineSegment(sketch, "E352", {"start": v(-10.43, 13.81) * mm, "end": v(-10.48, 13.82) * mm});
            skLineSegment(sketch, "E353", {"start": v(13.53, 14.93) * mm, "end": v(13.45, 14.95) * mm});
            skLineSegment(sketch, "E354", {"start": v(-0.79, -3.56) * mm, "end": v(-0.96, -3.52) * mm});
            skLineSegment(sketch, "E355", {"start": v(0.96, 3.52) * mm, "end": v(0.79, 3.56) * mm});
            skLineSegment(sketch, "E356", {"start": v(-13.03, -13.83) * mm, "end": v(-13.07, -13.82) * mm});
            skLineSegment(sketch, "E357", {"start": v(10.52, -13.83) * mm, "end": v(10.48, -13.82) * mm});
            skLineSegment(sketch, "E358", {"start": v(-10.48, -9.73) * mm, "end": v(-10.52, -9.72) * mm});
            skLineSegment(sketch, "E359", {"start": v(13.07, -9.73) * mm, "end": v(13.03, -9.72) * mm});
            skLineSegment(sketch, "E360", {"start": v(10.52, 9.72) * mm, "end": v(10.48, 9.73) * mm});
            skLineSegment(sketch, "E361", {"start": v(-13.03, 9.72) * mm, "end": v(-13.07, 9.73) * mm});
            skLineSegment(sketch, "E362", {"start": v(13.07, 13.82) * mm, "end": v(13.03, 13.83) * mm});
            skLineSegment(sketch, "E363", {"start": v(-10.48, 13.82) * mm, "end": v(-10.52, 13.83) * mm});
            skLineSegment(sketch, "E364", {"start": v(-13.36, -14.97) * mm, "end": v(-13.45, -14.95) * mm});
            skLineSegment(sketch, "E365", {"start": v(13.45, 14.95) * mm, "end": v(13.36, 14.97) * mm});
            skLineSegment(sketch, "E366", {"start": v(-0.61, -3.6) * mm, "end": v(-0.79, -3.56) * mm});
            skLineSegment(sketch, "E367", {"start": v(0.79, 3.56) * mm, "end": v(0.61, 3.6) * mm});
            skLineSegment(sketch, "E368", {"start": v(10.57, -13.84) * mm, "end": v(10.52, -13.83) * mm});
            skLineSegment(sketch, "E369", {"start": v(-10.52, -9.72) * mm, "end": v(-10.57, -9.7) * mm});
            skLineSegment(sketch, "E370", {"start": v(10.57, 9.7) * mm, "end": v(10.52, 9.72) * mm});
            skLineSegment(sketch, "E371", {"start": v(-10.52, 13.83) * mm, "end": v(-10.57, 13.84) * mm});
            skLineSegment(sketch, "E372", {"start": v(-13.27, -14.98) * mm, "end": v(-13.36, -14.97) * mm});
            skLineSegment(sketch, "E373", {"start": v(13.36, 14.97) * mm, "end": v(13.27, 14.98) * mm});
            skLineSegment(sketch, "E374", {"start": v(-12.98, -13.84) * mm, "end": v(-13.03, -13.83) * mm});
            skLineSegment(sketch, "E375", {"start": v(13.03, -9.72) * mm, "end": v(12.98, -9.7) * mm});
            skLineSegment(sketch, "E376", {"start": v(-12.98, 9.7) * mm, "end": v(-13.03, 9.72) * mm});
            skLineSegment(sketch, "E377", {"start": v(13.03, 13.83) * mm, "end": v(12.98, 13.84) * mm});
            skLineSegment(sketch, "E378", {"start": v(-0.44, -3.62) * mm, "end": v(-0.61, -3.6) * mm});
            skLineSegment(sketch, "E379", {"start": v(0.61, 3.6) * mm, "end": v(0.44, 3.62) * mm});
            skLineSegment(sketch, "E380", {"start": v(12.98, -9.7) * mm, "end": v(12.94, -9.7) * mm});
            skLineSegment(sketch, "E381", {"start": v(-12.94, 9.7) * mm, "end": v(-12.98, 9.7) * mm});
            skLineSegment(sketch, "E382", {"start": v(-10.57, -9.7) * mm, "end": v(-10.61, -9.7) * mm});
            skLineSegment(sketch, "E383", {"start": v(10.61, 9.7) * mm, "end": v(10.57, 9.7) * mm});
            skLineSegment(sketch, "E384", {"start": v(-13.18, -15) * mm, "end": v(-13.27, -14.98) * mm});
            skLineSegment(sketch, "E385", {"start": v(13.27, 14.98) * mm, "end": v(13.18, 15) * mm});
            skLineSegment(sketch, "E386", {"start": v(-12.94, -13.85) * mm, "end": v(-12.98, -13.84) * mm});
            skLineSegment(sketch, "E387", {"start": v(12.98, 13.84) * mm, "end": v(12.94, 13.85) * mm});
            skLineSegment(sketch, "E388", {"start": v(10.61, -13.85) * mm, "end": v(10.57, -13.84) * mm});
            skLineSegment(sketch, "E389", {"start": v(-10.57, 13.84) * mm, "end": v(-10.61, 13.85) * mm});
            skLineSegment(sketch, "E390", {"start": v(-0.26, -3.64) * mm, "end": v(-0.44, -3.62) * mm});
            skLineSegment(sketch, "E391", {"start": v(0.44, 3.62) * mm, "end": v(0.26, 3.64) * mm});
            skLineSegment(sketch, "E392", {"start": v(-13.09, -15) * mm, "end": v(-13.18, -15) * mm});
            skLineSegment(sketch, "E393", {"start": v(-12.9, -13.85) * mm, "end": v(-12.94, -13.85) * mm});
            skLineSegment(sketch, "E394", {"start": v(10.66, -13.85) * mm, "end": v(10.61, -13.85) * mm});
            skLineSegment(sketch, "E395", {"start": v(12.94, 13.85) * mm, "end": v(12.9, 13.85) * mm});
            skLineSegment(sketch, "E396", {"start": v(-10.61, 13.85) * mm, "end": v(-10.66, 13.85) * mm});
            skLineSegment(sketch, "E397", {"start": v(13.18, 15) * mm, "end": v(13.09, 15) * mm});
            skLineSegment(sketch, "E398", {"start": v(-10.61, -9.7) * mm, "end": v(-10.66, -9.7) * mm});
            skLineSegment(sketch, "E399", {"start": v(12.94, -9.7) * mm, "end": v(12.9, -9.7) * mm});
            skLineSegment(sketch, "E400", {"start": v(10.66, 9.7) * mm, "end": v(10.61, 9.7) * mm});
            skLineSegment(sketch, "E401", {"start": v(-12.9, 9.7) * mm, "end": v(-12.94, 9.7) * mm});
            skLineSegment(sketch, "E402", {"start": v(-0.09, -3.65) * mm, "end": v(-0.26, -3.64) * mm});
            skLineSegment(sketch, "E403", {"start": v(0.26, 3.64) * mm, "end": v(0.09, 3.65) * mm});
            skLineSegment(sketch, "E404", {"start": v(-13, -15) * mm, "end": v(-13.09, -15) * mm});
            skLineSegment(sketch, "E405", {"start": v(-12.85, -13.85) * mm, "end": v(-12.9, -13.85) * mm});
            skLineSegment(sketch, "E406", {"start": v(10.7, -13.85) * mm, "end": v(10.66, -13.85) * mm});
            skLineSegment(sketch, "E407", {"start": v(-10.66, -9.7) * mm, "end": v(-10.7, -9.7) * mm});
            skLineSegment(sketch, "E408", {"start": v(12.9, -9.7) * mm, "end": v(12.85, -9.7) * mm});
            skLineSegment(sketch, "E409", {"start": v(10.7, 9.7) * mm, "end": v(10.66, 9.7) * mm});
            skLineSegment(sketch, "E410", {"start": v(-12.85, 9.7) * mm, "end": v(-12.9, 9.7) * mm});
            skLineSegment(sketch, "E411", {"start": v(12.9, 13.85) * mm, "end": v(12.85, 13.85) * mm});
            skLineSegment(sketch, "E412", {"start": v(-10.66, 13.85) * mm, "end": v(-10.7, 13.85) * mm});
            skLineSegment(sketch, "E413", {"start": v(13.09, 15) * mm, "end": v(13, 15) * mm});
            skLineSegment(sketch, "E414", {"start": v(8.25, -12.8) * mm, "end": v(4, -12.8) * mm});
            skLineSegment(sketch, "E415", {"start": v(-4, 12.8) * mm, "end": v(-8.25, 12.8) * mm});
            skLineSegment(sketch, "E416", {"start": v(-13, -15) * mm, "end": v(-4.5, -15) * mm});
            skLineSegment(sketch, "E417", {"start": v(4.5, -15) * mm, "end": v(13, -15) * mm});
            skLineSegment(sketch, "E418", {"start": v(-4.5, -14.5) * mm, "end": v(-4, -14.5) * mm});
            skLineSegment(sketch, "E419", {"start": v(4, -14.5) * mm, "end": v(4.5, -14.5) * mm});
            skLineSegment(sketch, "E420", {"start": v(-12.85, -13.85) * mm, "end": v(-10.7, -13.85) * mm});
            skLineSegment(sketch, "E421", {"start": v(10.7, -13.85) * mm, "end": v(12.85, -13.85) * mm});
            skLineSegment(sketch, "E422", {"start": v(-12.85, -9.7) * mm, "end": v(-10.7, -9.7) * mm});
            skLineSegment(sketch, "E423", {"start": v(10.7, -9.7) * mm, "end": v(12.85, -9.7) * mm});
            skLineSegment(sketch, "E424", {"start": v(-12.8, -8.25) * mm, "end": v(-10.05, -8.25) * mm});
            skLineSegment(sketch, "E425", {"start": v(10.05, -8.25) * mm, "end": v(12.8, -8.25) * mm});
            skLineSegment(sketch, "E426", {"start": v(-4.2, -6) * mm, "end": v(-0.92, -6) * mm});
            skLineSegment(sketch, "E427", {"start": v(0.92, -6) * mm, "end": v(4.2, -6) * mm});
            skLineSegment(sketch, "E428", {"start": v(-15, -4.5) * mm, "end": v(-14.5, -4.5) * mm});
            skLineSegment(sketch, "E429", {"start": v(14.5, -4.5) * mm, "end": v(15, -4.5) * mm});
            skLineSegment(sketch, "E430", {"start": v(-14.5, -4) * mm, "end": v(-12.8, -4) * mm});
            skLineSegment(sketch, "E431", {"start": v(12.8, -4) * mm, "end": v(14.5, -4) * mm});
            skLineSegment(sketch, "E432", {"start": v(-0.09, -3.65) * mm, "end": v(0.09, -3.65) * mm});
            skLineSegment(sketch, "E433", {"start": v(-0.09, 3.65) * mm, "end": v(0.09, 3.65) * mm});
            skLineSegment(sketch, "E434", {"start": v(12.8, 4) * mm, "end": v(14.5, 4) * mm});
            skLineSegment(sketch, "E435", {"start": v(-14.5, 4) * mm, "end": v(-12.8, 4) * mm});
            skLineSegment(sketch, "E436", {"start": v(14.5, 4.5) * mm, "end": v(15, 4.5) * mm});
            skLineSegment(sketch, "E437", {"start": v(-15, 4.5) * mm, "end": v(-14.5, 4.5) * mm});
            skLineSegment(sketch, "E438", {"start": v(0.92, 6) * mm, "end": v(4.2, 6) * mm});
            skLineSegment(sketch, "E439", {"start": v(-4.2, 6) * mm, "end": v(-0.92, 6) * mm});
            skLineSegment(sketch, "E440", {"start": v(10.05, 8.25) * mm, "end": v(12.8, 8.25) * mm});
            skLineSegment(sketch, "E441", {"start": v(-12.8, 8.25) * mm, "end": v(-10.05, 8.25) * mm});
            skLineSegment(sketch, "E442", {"start": v(10.7, 9.7) * mm, "end": v(12.85, 9.7) * mm});
            skLineSegment(sketch, "E443", {"start": v(-12.85, 9.7) * mm, "end": v(-10.7, 9.7) * mm});
            skLineSegment(sketch, "E444", {"start": v(10.7, 13.85) * mm, "end": v(12.85, 13.85) * mm});
            skLineSegment(sketch, "E445", {"start": v(-12.85, 13.85) * mm, "end": v(-10.7, 13.85) * mm});
            skLineSegment(sketch, "E446", {"start": v(4, 14.5) * mm, "end": v(4.5, 14.5) * mm});
            skLineSegment(sketch, "E447", {"start": v(-4.5, 14.5) * mm, "end": v(-4, 14.5) * mm});
            skLineSegment(sketch, "E448", {"start": v(4.5, 15) * mm, "end": v(13, 15) * mm});
            skLineSegment(sketch, "E449", {"start": v(-13, 15) * mm, "end": v(-4.5, 15) * mm});
            skLineSegment(sketch, "E450", {"start": v(-8.25, -12.8) * mm, "end": v(-4, -12.8) * mm});
            skLineSegment(sketch, "E451", {"start": v(4, 12.8) * mm, "end": v(8.25, 12.8) * mm});
            skLineSegment(sketch, "E452", {"start": v(13, -15) * mm, "end": v(13.09, -15) * mm});
            skLineSegment(sketch, "E453", {"start": v(-10.7, -13.85) * mm, "end": v(-10.66, -13.85) * mm});
            skLineSegment(sketch, "E454", {"start": v(12.85, -13.85) * mm, "end": v(12.9, -13.85) * mm});
            skLineSegment(sketch, "E455", {"start": v(-12.9, -9.7) * mm, "end": v(-12.85, -9.7) * mm});
            skLineSegment(sketch, "E456", {"start": v(10.66, -9.7) * mm, "end": v(10.7, -9.7) * mm});
            skLineSegment(sketch, "E457", {"start": v(12.85, 9.7) * mm, "end": v(12.9, 9.7) * mm});
            skLineSegment(sketch, "E458", {"start": v(-10.7, 9.7) * mm, "end": v(-10.66, 9.7) * mm});
            skLineSegment(sketch, "E459", {"start": v(10.66, 13.85) * mm, "end": v(10.7, 13.85) * mm});
            skLineSegment(sketch, "E460", {"start": v(-12.9, 13.85) * mm, "end": v(-12.85, 13.85) * mm});
            skLineSegment(sketch, "E461", {"start": v(-13.09, 15) * mm, "end": v(-13, 15) * mm});
            skLineSegment(sketch, "E462", {"start": v(0.09, -3.65) * mm, "end": v(0.26, -3.64) * mm});
            skLineSegment(sketch, "E463", {"start": v(-0.26, 3.64) * mm, "end": v(-0.09, 3.65) * mm});
            skLineSegment(sketch, "E464", {"start": v(-12.94, -9.7) * mm, "end": v(-12.9, -9.7) * mm});
            skLineSegment(sketch, "E465", {"start": v(10.61, -9.7) * mm, "end": v(10.66, -9.7) * mm});
            skLineSegment(sketch, "E466", {"start": v(12.9, 9.7) * mm, "end": v(12.94, 9.7) * mm});
            skLineSegment(sketch, "E467", {"start": v(-10.66, 9.7) * mm, "end": v(-10.61, 9.7) * mm});
            skLineSegment(sketch, "E468", {"start": v(13.09, -15) * mm, "end": v(13.18, -15) * mm});
            skLineSegment(sketch, "E469", {"start": v(-10.66, -13.85) * mm, "end": v(-10.61, -13.85) * mm});
            skLineSegment(sketch, "E470", {"start": v(12.9, -13.85) * mm, "end": v(12.94, -13.85) * mm});
            skLineSegment(sketch, "E471", {"start": v(10.61, 13.85) * mm, "end": v(10.66, 13.85) * mm});
            skLineSegment(sketch, "E472", {"start": v(-12.94, 13.85) * mm, "end": v(-12.9, 13.85) * mm});
            skLineSegment(sketch, "E473", {"start": v(-13.18, 15) * mm, "end": v(-13.09, 15) * mm});
            skLineSegment(sketch, "E474", {"start": v(0.26, -3.64) * mm, "end": v(0.44, -3.62) * mm});
            skLineSegment(sketch, "E475", {"start": v(-0.44, 3.62) * mm, "end": v(-0.26, 3.64) * mm});
            skLineSegment(sketch, "E476", {"start": v(-10.61, -13.85) * mm, "end": v(-10.57, -13.84) * mm});
            skLineSegment(sketch, "E477", {"start": v(10.57, 13.84) * mm, "end": v(10.61, 13.85) * mm});
            skLineSegment(sketch, "E478", {"start": v(12.94, -13.85) * mm, "end": v(12.98, -13.84) * mm});
            skLineSegment(sketch, "E479", {"start": v(-12.98, 13.84) * mm, "end": v(-12.94, 13.85) * mm});
            skLineSegment(sketch, "E480", {"start": v(13.18, -15) * mm, "end": v(13.27, -14.98) * mm});
            skLineSegment(sketch, "E481", {"start": v(-13.27, 14.98) * mm, "end": v(-13.18, 15) * mm});
            skLineSegment(sketch, "E482", {"start": v(10.57, -9.7) * mm, "end": v(10.61, -9.7) * mm});
            skLineSegment(sketch, "E483", {"start": v(-10.61, 9.7) * mm, "end": v(-10.57, 9.7) * mm});
            skLineSegment(sketch, "E484", {"start": v(-12.98, -9.7) * mm, "end": v(-12.94, -9.7) * mm});
            skLineSegment(sketch, "E485", {"start": v(12.94, 9.7) * mm, "end": v(12.98, 9.7) * mm});
            skLineSegment(sketch, "E486", {"start": v(0.44, -3.62) * mm, "end": v(0.61, -3.6) * mm});
            skLineSegment(sketch, "E487", {"start": v(-0.61, 3.6) * mm, "end": v(-0.44, 3.62) * mm});
            skLineSegment(sketch, "E488", {"start": v(12.98, -13.84) * mm, "end": v(13.03, -13.83) * mm});
            skLineSegment(sketch, "E489", {"start": v(-13.03, -9.72) * mm, "end": v(-12.98, -9.7) * mm});
            skLineSegment(sketch, "E490", {"start": v(12.98, 9.7) * mm, "end": v(13.03, 9.72) * mm});
            skLineSegment(sketch, "E491", {"start": v(-13.03, 13.83) * mm, "end": v(-12.98, 13.84) * mm});
            skLineSegment(sketch, "E492", {"start": v(13.27, -14.98) * mm, "end": v(13.36, -14.97) * mm});
            skLineSegment(sketch, "E493", {"start": v(-13.36, 14.97) * mm, "end": v(-13.27, 14.98) * mm});
            skLineSegment(sketch, "E494", {"start": v(-10.57, -13.84) * mm, "end": v(-10.52, -13.83) * mm});
            skLineSegment(sketch, "E495", {"start": v(10.52, -9.72) * mm, "end": v(10.57, -9.7) * mm});
            skLineSegment(sketch, "E496", {"start": v(-10.57, 9.7) * mm, "end": v(-10.52, 9.72) * mm});
            skLineSegment(sketch, "E497", {"start": v(10.52, 13.83) * mm, "end": v(10.57, 13.84) * mm});
            skLineSegment(sketch, "E498", {"start": v(0.61, -3.6) * mm, "end": v(0.79, -3.56) * mm});
            skLineSegment(sketch, "E499", {"start": v(-0.79, 3.56) * mm, "end": v(-0.61, 3.6) * mm});
            skLineSegment(sketch, "E500", {"start": v(13.36, -14.97) * mm, "end": v(13.45, -14.95) * mm});
            skLineSegment(sketch, "E501", {"start": v(-13.45, 14.95) * mm, "end": v(-13.36, 14.97) * mm});
            skLineSegment(sketch, "E502", {"start": v(-10.52, -13.83) * mm, "end": v(-10.48, -13.82) * mm});
            skLineSegment(sketch, "E503", {"start": v(13.03, -13.83) * mm, "end": v(13.07, -13.82) * mm});
            skLineSegment(sketch, "E504", {"start": v(-13.07, -9.73) * mm, "end": v(-13.03, -9.72) * mm});
            skLineSegment(sketch, "E505", {"start": v(10.48, -9.73) * mm, "end": v(10.52, -9.72) * mm});
            skLineSegment(sketch, "E506", {"start": v(13.03, 9.72) * mm, "end": v(13.07, 9.73) * mm});
            skLineSegment(sketch, "E507", {"start": v(-10.52, 9.72) * mm, "end": v(-10.48, 9.73) * mm});
            skLineSegment(sketch, "E508", {"start": v(10.48, 13.82) * mm, "end": v(10.52, 13.83) * mm});
            skLineSegment(sketch, "E509", {"start": v(-13.07, 13.82) * mm, "end": v(-13.03, 13.83) * mm});
            skLineSegment(sketch, "E510", {"start": v(0.79, -3.56) * mm, "end": v(0.96, -3.52) * mm});
            skLineSegment(sketch, "E511", {"start": v(-0.96, 3.52) * mm, "end": v(-0.79, 3.56) * mm});
            skLineSegment(sketch, "E512", {"start": v(13.45, -14.95) * mm, "end": v(13.53, -14.93) * mm});
            skLineSegment(sketch, "E513", {"start": v(-10.48, -13.82) * mm, "end": v(-10.43, -13.81) * mm});
            skLineSegment(sketch, "E514", {"start": v(10.43, -9.74) * mm, "end": v(10.48, -9.73) * mm});
            skLineSegment(sketch, "E515", {"start": v(-10.48, 9.73) * mm, "end": v(-10.43, 9.74) * mm});
            skLineSegment(sketch, "E516", {"start": v(10.43, 13.81) * mm, "end": v(10.48, 13.82) * mm});
            skLineSegment(sketch, "E517", {"start": v(-13.53, 14.93) * mm, "end": v(-13.45, 14.95) * mm});
            skLineSegment(sketch, "E518", {"start": v(13.07, -13.82) * mm, "end": v(13.12, -13.81) * mm});
            skLineSegment(sketch, "E519", {"start": v(-13.12, -9.74) * mm, "end": v(-13.07, -9.73) * mm});
            skLineSegment(sketch, "E520", {"start": v(13.07, 9.73) * mm, "end": v(13.12, 9.74) * mm});
            skLineSegment(sketch, "E521", {"start": v(-13.12, 13.81) * mm, "end": v(-13.07, 13.82) * mm});
            skLineSegment(sketch, "E522", {"start": v(0.96, -3.52) * mm, "end": v(1.13, -3.47) * mm});
            skLineSegment(sketch, "E523", {"start": v(-1.13, 3.47) * mm, "end": v(-0.96, 3.52) * mm});
            skLineSegment(sketch, "E524", {"start": v(13.12, -13.81) * mm, "end": v(13.16, -13.8) * mm});
            skLineSegment(sketch, "E525", {"start": v(-13.16, -9.75) * mm, "end": v(-13.12, -9.74) * mm});
            skLineSegment(sketch, "E526", {"start": v(13.12, 9.74) * mm, "end": v(13.16, 9.75) * mm});
            skLineSegment(sketch, "E527", {"start": v(-13.16, 13.8) * mm, "end": v(-13.12, 13.81) * mm});
            skLineSegment(sketch, "E528", {"start": v(-10.43, -13.81) * mm, "end": v(-10.4, -13.8) * mm});
            skLineSegment(sketch, "E529", {"start": v(10.4, -9.75) * mm, "end": v(10.43, -9.74) * mm});
            skLineSegment(sketch, "E530", {"start": v(-10.43, 9.74) * mm, "end": v(-10.4, 9.75) * mm});
            skLineSegment(sketch, "E531", {"start": v(10.4, 13.8) * mm, "end": v(10.43, 13.81) * mm});
            skLineSegment(sketch, "E532", {"start": v(13.53, -14.93) * mm, "end": v(13.62, -14.9) * mm});
            skLineSegment(sketch, "E533", {"start": v(-13.62, 14.9) * mm, "end": v(-13.53, 14.93) * mm});
            skLineSegment(sketch, "E534", {"start": v(13.62, -14.9) * mm, "end": v(13.7, -14.87) * mm});
            skLineSegment(sketch, "E535", {"start": v(-13.7, 14.87) * mm, "end": v(-13.62, 14.9) * mm});
            skLineSegment(sketch, "E536", {"start": v(-10.4, -13.8) * mm, "end": v(-10.35, -13.79) * mm});
            skLineSegment(sketch, "E537", {"start": v(13.16, -13.8) * mm, "end": v(13.2, -13.79) * mm});
            skLineSegment(sketch, "E538", {"start": v(-13.2, -9.76) * mm, "end": v(-13.16, -9.75) * mm});
            skLineSegment(sketch, "E539", {"start": v(10.35, -9.76) * mm, "end": v(10.4, -9.75) * mm});
            skLineSegment(sketch, "E540", {"start": v(13.16, 9.75) * mm, "end": v(13.2, 9.76) * mm});
            skLineSegment(sketch, "E541", {"start": v(-10.4, 9.75) * mm, "end": v(-10.35, 9.76) * mm});
            skLineSegment(sketch, "E542", {"start": v(10.35, 13.79) * mm, "end": v(10.4, 13.8) * mm});
            skLineSegment(sketch, "E543", {"start": v(-13.2, 13.79) * mm, "end": v(-13.16, 13.8) * mm});
            skLineSegment(sketch, "E544", {"start": v(1.13, -3.47) * mm, "end": v(1.3, -3.41) * mm});
            skLineSegment(sketch, "E545", {"start": v(-1.3, 3.41) * mm, "end": v(-1.13, 3.47) * mm});
            skLineSegment(sketch, "E546", {"start": v(13.7, -14.87) * mm, "end": v(13.79, -14.84) * mm});
            skLineSegment(sketch, "E547", {"start": v(-13.79, 14.84) * mm, "end": v(-13.7, 14.87) * mm});
            skLineSegment(sketch, "E548", {"start": v(-13.24, -9.78) * mm, "end": v(-13.2, -9.76) * mm});
            skLineSegment(sketch, "E549", {"start": v(10.3, -9.78) * mm, "end": v(10.35, -9.76) * mm});
            skLineSegment(sketch, "E550", {"start": v(13.2, 9.76) * mm, "end": v(13.24, 9.78) * mm});
            skLineSegment(sketch, "E551", {"start": v(-10.35, 9.76) * mm, "end": v(-10.3, 9.78) * mm});
            skLineSegment(sketch, "E552", {"start": v(-10.35, -13.79) * mm, "end": v(-10.3, -13.77) * mm});
            skLineSegment(sketch, "E553", {"start": v(13.2, -13.79) * mm, "end": v(13.24, -13.77) * mm});
            skLineSegment(sketch, "E554", {"start": v(10.3, 13.77) * mm, "end": v(10.35, 13.79) * mm});
            skLineSegment(sketch, "E555", {"start": v(-13.24, 13.77) * mm, "end": v(-13.2, 13.79) * mm});
            skLineSegment(sketch, "E556", {"start": v(1.3, -3.41) * mm, "end": v(1.46, -3.35) * mm});
            skLineSegment(sketch, "E557", {"start": v(-1.46, 3.35) * mm, "end": v(-1.3, 3.41) * mm});
            skLineSegment(sketch, "E558", {"start": v(-10.3, -13.77) * mm, "end": v(-10.27, -13.75) * mm});
            skLineSegment(sketch, "E559", {"start": v(13.24, -13.77) * mm, "end": v(13.28, -13.75) * mm});
            skLineSegment(sketch, "E560", {"start": v(10.27, 13.75) * mm, "end": v(10.3, 13.77) * mm});
            skLineSegment(sketch, "E561", {"start": v(-13.28, 13.75) * mm, "end": v(-13.24, 13.77) * mm});
            skLineSegment(sketch, "E562", {"start": v(-13.28, -9.8) * mm, "end": v(-13.24, -9.78) * mm});
            skLineSegment(sketch, "E563", {"start": v(10.27, -9.8) * mm, "end": v(10.3, -9.78) * mm});
            skLineSegment(sketch, "E564", {"start": v(13.24, 9.78) * mm, "end": v(13.28, 9.8) * mm});
            skLineSegment(sketch, "E565", {"start": v(-10.3, 9.78) * mm, "end": v(-10.27, 9.8) * mm});
            skLineSegment(sketch, "E566", {"start": v(13.79, -14.84) * mm, "end": v(13.87, -14.8) * mm});
            skLineSegment(sketch, "E567", {"start": v(-13.87, 14.8) * mm, "end": v(-13.79, 14.84) * mm});
            skLineSegment(sketch, "E568", {"start": v(1.46, -3.35) * mm, "end": v(1.62, -3.27) * mm});
            skLineSegment(sketch, "E569", {"start": v(-1.62, 3.27) * mm, "end": v(-1.46, 3.35) * mm});
            skLineSegment(sketch, "E570", {"start": v(-10.27, -13.75) * mm, "end": v(-10.23, -13.73) * mm});
            skLineSegment(sketch, "E571", {"start": v(13.28, -13.75) * mm, "end": v(13.32, -13.73) * mm});
            skLineSegment(sketch, "E572", {"start": v(10.23, 13.73) * mm, "end": v(10.27, 13.75) * mm});
            skLineSegment(sketch, "E573", {"start": v(-13.32, 13.73) * mm, "end": v(-13.28, 13.75) * mm});
            skLineSegment(sketch, "E574", {"start": v(13.87, -14.8) * mm, "end": v(13.95, -14.76) * mm});
            skLineSegment(sketch, "E575", {"start": v(-13.95, 14.76) * mm, "end": v(-13.87, 14.8) * mm});
            skLineSegment(sketch, "E576", {"start": v(-13.32, -9.82) * mm, "end": v(-13.28, -9.8) * mm});
            skLineSegment(sketch, "E577", {"start": v(10.23, -9.82) * mm, "end": v(10.27, -9.8) * mm});
            skLineSegment(sketch, "E578", {"start": v(13.28, 9.8) * mm, "end": v(13.32, 9.82) * mm});
            skLineSegment(sketch, "E579", {"start": v(-10.27, 9.8) * mm, "end": v(-10.23, 9.82) * mm});
            skLineSegment(sketch, "E580", {"start": v(10.19, -9.84) * mm, "end": v(10.23, -9.82) * mm});
            skLineSegment(sketch, "E581", {"start": v(-10.23, 9.82) * mm, "end": v(-10.19, 9.84) * mm});
            skLineSegment(sketch, "E582", {"start": v(-13.36, -9.84) * mm, "end": v(-13.32, -9.82) * mm});
            skLineSegment(sketch, "E583", {"start": v(13.32, 9.82) * mm, "end": v(13.36, 9.84) * mm});
            skLineSegment(sketch, "E584", {"start": v(13.95, -14.76) * mm, "end": v(14.03, -14.72) * mm});
            skLineSegment(sketch, "E585", {"start": v(-14.03, 14.72) * mm, "end": v(-13.95, 14.76) * mm});
            skLineSegment(sketch, "E586", {"start": v(-10.23, -13.73) * mm, "end": v(-10.19, -13.7) * mm});
            skLineSegment(sketch, "E587", {"start": v(10.19, 13.7) * mm, "end": v(10.23, 13.73) * mm});
            skLineSegment(sketch, "E588", {"start": v(13.32, -13.73) * mm, "end": v(13.36, -13.7) * mm});
            skLineSegment(sketch, "E589", {"start": v(-13.36, 13.7) * mm, "end": v(-13.32, 13.73) * mm});
            skLineSegment(sketch, "E590", {"start": v(-0.92, -6) * mm, "end": v(0, -5.47) * mm});
            skLineSegment(sketch, "E591", {"start": v(0, 5.47) * mm, "end": v(0.92, 6) * mm});
            skLineSegment(sketch, "E592", {"start": v(13.36, -13.7) * mm, "end": v(13.4, -13.68) * mm});
            skLineSegment(sketch, "E593", {"start": v(-13.4, 13.68) * mm, "end": v(-13.36, 13.7) * mm});
            skLineSegment(sketch, "E594", {"start": v(-10.19, -13.7) * mm, "end": v(-10.15, -13.68) * mm});
            skLineSegment(sketch, "E595", {"start": v(10.15, 13.68) * mm, "end": v(10.19, 13.7) * mm});
            skLineSegment(sketch, "E596", {"start": v(14.03, -14.72) * mm, "end": v(14.1, -14.67) * mm});
            skLineSegment(sketch, "E597", {"start": v(-14.1, 14.67) * mm, "end": v(-14.03, 14.72) * mm});
            skLineSegment(sketch, "E598", {"start": v(-13.4, -9.87) * mm, "end": v(-13.36, -9.84) * mm});
            skLineSegment(sketch, "E599", {"start": v(13.36, 9.84) * mm, "end": v(13.4, 9.87) * mm});
            skLineSegment(sketch, "E600", {"start": v(10.15, -9.87) * mm, "end": v(10.19, -9.84) * mm});
            skLineSegment(sketch, "E601", {"start": v(-10.19, 9.84) * mm, "end": v(-10.15, 9.87) * mm});
            skLineSegment(sketch, "E602", {"start": v(-10.15, -13.68) * mm, "end": v(-10.11, -13.66) * mm});
            skLineSegment(sketch, "E603", {"start": v(13.4, -13.68) * mm, "end": v(13.44, -13.66) * mm});
            skLineSegment(sketch, "E604", {"start": v(-13.44, -9.9) * mm, "end": v(-13.4, -9.87) * mm});
            skLineSegment(sketch, "E605", {"start": v(10.11, -9.9) * mm, "end": v(10.15, -9.87) * mm});
            skLineSegment(sketch, "E606", {"start": v(13.4, 9.87) * mm, "end": v(13.44, 9.9) * mm});
            skLineSegment(sketch, "E607", {"start": v(-10.15, 9.87) * mm, "end": v(-10.11, 9.9) * mm});
            skLineSegment(sketch, "E608", {"start": v(10.11, 13.66) * mm, "end": v(10.15, 13.68) * mm});
            skLineSegment(sketch, "E609", {"start": v(-13.44, 13.66) * mm, "end": v(-13.4, 13.68) * mm});
            skLineSegment(sketch, "E610", {"start": v(14.1, -14.67) * mm, "end": v(14.18, -14.62) * mm});
            skLineSegment(sketch, "E611", {"start": v(-14.18, 14.62) * mm, "end": v(-14.1, 14.67) * mm});
            skLineSegment(sketch, "E612", {"start": v(3.12, -4.53) * mm, "end": v(3.35, -4.36) * mm});
            skLineSegment(sketch, "E613", {"start": v(-3.35, 4.36) * mm, "end": v(-3.12, 4.53) * mm});
            skLineSegment(sketch, "E614", {"start": v(-13.47, -9.92) * mm, "end": v(-13.44, -9.9) * mm});
            skLineSegment(sketch, "E615", {"start": v(10.08, -9.92) * mm, "end": v(10.11, -9.9) * mm});
            skLineSegment(sketch, "E616", {"start": v(13.44, 9.9) * mm, "end": v(13.47, 9.92) * mm});
            skLineSegment(sketch, "E617", {"start": v(-10.11, 9.9) * mm, "end": v(-10.08, 9.92) * mm});
            skLineSegment(sketch, "E618", {"start": v(14.18, -14.62) * mm, "end": v(14.25, -14.56) * mm});
            skLineSegment(sketch, "E619", {"start": v(-14.25, 14.56) * mm, "end": v(-14.18, 14.62) * mm});
            skLineSegment(sketch, "E620", {"start": v(-10.11, -13.66) * mm, "end": v(-10.08, -13.63) * mm});
            skLineSegment(sketch, "E621", {"start": v(13.44, -13.66) * mm, "end": v(13.47, -13.63) * mm});
            skLineSegment(sketch, "E622", {"start": v(10.08, 13.63) * mm, "end": v(10.11, 13.66) * mm});
            skLineSegment(sketch, "E623", {"start": v(-13.47, 13.63) * mm, "end": v(-13.44, 13.66) * mm});
            skLineSegment(sketch, "E624", {"start": v(3.35, -4.36) * mm, "end": v(3.57, -4.18) * mm});
            skLineSegment(sketch, "E625", {"start": v(-3.57, 4.18) * mm, "end": v(-3.35, 4.36) * mm});
            skLineSegment(sketch, "E626", {"start": v(14.25, -14.56) * mm, "end": v(14.32, -14.5) * mm});
            skLineSegment(sketch, "E627", {"start": v(-10.08, -13.63) * mm, "end": v(-10.04, -13.6) * mm});
            skLineSegment(sketch, "E628", {"start": v(10.04, 13.6) * mm, "end": v(10.08, 13.63) * mm});
            skLineSegment(sketch, "E629", {"start": v(-14.32, 14.5) * mm, "end": v(-14.25, 14.56) * mm});
            skLineSegment(sketch, "E630", {"start": v(13.47, -13.63) * mm, "end": v(13.5, -13.6) * mm});
            skLineSegment(sketch, "E631", {"start": v(-13.5, 13.6) * mm, "end": v(-13.47, 13.63) * mm});
            skLineSegment(sketch, "E632", {"start": v(10.04, -9.95) * mm, "end": v(10.08, -9.92) * mm});
            skLineSegment(sketch, "E633", {"start": v(-10.08, 9.92) * mm, "end": v(-10.04, 9.95) * mm});
            skLineSegment(sketch, "E634", {"start": v(-13.5, -9.95) * mm, "end": v(-13.47, -9.92) * mm});
            skLineSegment(sketch, "E635", {"start": v(13.47, 9.92) * mm, "end": v(13.5, 9.95) * mm});
            skLineSegment(sketch, "E636", {"start": v(-3.12, -4.53) * mm, "end": v(-1.62, -3.27) * mm});
            skLineSegment(sketch, "E637", {"start": v(1.62, 3.27) * mm, "end": v(3.12, 4.53) * mm});
            skLineSegment(sketch, "E638", {"start": v(3.57, -4.18) * mm, "end": v(3.79, -3.99) * mm});
            skLineSegment(sketch, "E639", {"start": v(-3.79, 3.99) * mm, "end": v(-3.57, 4.18) * mm});
            skLineSegment(sketch, "E640", {"start": v(-10.04, -13.6) * mm, "end": v(-10, -13.57) * mm});
            skLineSegment(sketch, "E641", {"start": v(13.5, -13.6) * mm, "end": v(13.54, -13.57) * mm});
            skLineSegment(sketch, "E642", {"start": v(-13.54, -9.98) * mm, "end": v(-13.5, -9.95) * mm});
            skLineSegment(sketch, "E643", {"start": v(10, -9.98) * mm, "end": v(10.04, -9.95) * mm});
            skLineSegment(sketch, "E644", {"start": v(13.5, 9.95) * mm, "end": v(13.54, 9.98) * mm});
            skLineSegment(sketch, "E645", {"start": v(-10.04, 9.95) * mm, "end": v(-10, 9.98) * mm});
            skLineSegment(sketch, "E646", {"start": v(10, 13.57) * mm, "end": v(10.04, 13.6) * mm});
            skLineSegment(sketch, "E647", {"start": v(-13.54, 13.57) * mm, "end": v(-13.5, 13.6) * mm});
            skLineSegment(sketch, "E648", {"start": v(14.32, -14.5) * mm, "end": v(14.38, -14.45) * mm});
            skLineSegment(sketch, "E649", {"start": v(-14.38, 14.45) * mm, "end": v(-14.32, 14.5) * mm});
            skLineSegment(sketch, "E650", {"start": v(-13.57, -10) * mm, "end": v(-13.54, -9.98) * mm});
            skLineSegment(sketch, "E651", {"start": v(13.54, 9.98) * mm, "end": v(13.57, 10) * mm});
            skLineSegment(sketch, "E652", {"start": v(14.38, -14.45) * mm, "end": v(14.45, -14.38) * mm});
            skLineSegment(sketch, "E653", {"start": v(13.54, -13.57) * mm, "end": v(13.57, -13.54) * mm});
            skLineSegment(sketch, "E654", {"start": v(-8.25, -10.05) * mm, "end": v(-4.2, -6) * mm});
            skLineSegment(sketch, "E655", {"start": v(9.98, -10) * mm, "end": v(10, -9.98) * mm});
            skLineSegment(sketch, "E656", {"start": v(-10.05, -8.25) * mm, "end": v(-6, -4.2) * mm});
            skLineSegment(sketch, "E657", {"start": v(3.79, -3.99) * mm, "end": v(3.99, -3.79) * mm});
            skLineSegment(sketch, "E658", {"start": v(-3.99, 3.79) * mm, "end": v(-3.79, 3.99) * mm});
            skLineSegment(sketch, "E659", {"start": v(6, 4.2) * mm, "end": v(10.05, 8.25) * mm});
            skLineSegment(sketch, "E660", {"start": v(4.2, 6) * mm, "end": v(8.25, 10.05) * mm});
            skLineSegment(sketch, "E661", {"start": v(-10, 9.98) * mm, "end": v(-9.98, 10) * mm});
            skLineSegment(sketch, "E662", {"start": v(-13.57, 13.54) * mm, "end": v(-13.54, 13.57) * mm});
            skLineSegment(sketch, "E663", {"start": v(-14.45, 14.38) * mm, "end": v(-14.38, 14.45) * mm});
            skLineSegment(sketch, "E664", {"start": v(-10, -13.57) * mm, "end": v(-9.98, -13.54) * mm});
            skLineSegment(sketch, "E665", {"start": v(9.98, 13.54) * mm, "end": v(10, 13.57) * mm});
            skLineSegment(sketch, "E666", {"start": v(14.45, -14.38) * mm, "end": v(14.5, -14.32) * mm});
            skLineSegment(sketch, "E667", {"start": v(-14.5, 14.32) * mm, "end": v(-14.45, 14.38) * mm});
            skLineSegment(sketch, "E668", {"start": v(-9.98, -13.54) * mm, "end": v(-9.95, -13.5) * mm});
            skLineSegment(sketch, "E669", {"start": v(13.57, -13.54) * mm, "end": v(13.6, -13.5) * mm});
            skLineSegment(sketch, "E670", {"start": v(-13.6, -10.04) * mm, "end": v(-13.57, -10) * mm});
            skLineSegment(sketch, "E671", {"start": v(9.95, -10.04) * mm, "end": v(9.98, -10) * mm});
            skLineSegment(sketch, "E672", {"start": v(13.57, 10) * mm, "end": v(13.6, 10.04) * mm});
            skLineSegment(sketch, "E673", {"start": v(-9.98, 10) * mm, "end": v(-9.95, 10.04) * mm});
            skLineSegment(sketch, "E674", {"start": v(9.95, 13.5) * mm, "end": v(9.98, 13.54) * mm});
            skLineSegment(sketch, "E675", {"start": v(-13.6, 13.5) * mm, "end": v(-13.57, 13.54) * mm});
            skLineSegment(sketch, "E676", {"start": v(3.99, -3.79) * mm, "end": v(4.18, -3.57) * mm});
            skLineSegment(sketch, "E677", {"start": v(-4.18, 3.57) * mm, "end": v(-3.99, 3.79) * mm});
            skLineSegment(sketch, "E678", {"start": v(-4.53, -3.12) * mm, "end": v(-3.27, -1.62) * mm});
            skLineSegment(sketch, "E679", {"start": v(3.27, 1.62) * mm, "end": v(4.53, 3.12) * mm});
            skLineSegment(sketch, "E680", {"start": v(-9.95, -13.5) * mm, "end": v(-9.92, -13.47) * mm});
            skLineSegment(sketch, "E681", {"start": v(9.92, 13.47) * mm, "end": v(9.95, 13.5) * mm});
            skLineSegment(sketch, "E682", {"start": v(9.92, -10.08) * mm, "end": v(9.95, -10.04) * mm});
            skLineSegment(sketch, "E683", {"start": v(-9.95, 10.04) * mm, "end": v(-9.92, 10.08) * mm});
            skLineSegment(sketch, "E684", {"start": v(13.6, -13.5) * mm, "end": v(13.63, -13.47) * mm});
            skLineSegment(sketch, "E685", {"start": v(-13.63, 13.47) * mm, "end": v(-13.6, 13.5) * mm});
            skLineSegment(sketch, "E686", {"start": v(14.5, -14.32) * mm, "end": v(14.56, -14.25) * mm});
            skLineSegment(sketch, "E687", {"start": v(-13.63, -10.08) * mm, "end": v(-13.6, -10.04) * mm});
            skLineSegment(sketch, "E688", {"start": v(13.6, 10.04) * mm, "end": v(13.63, 10.08) * mm});
            skLineSegment(sketch, "E689", {"start": v(-14.56, 14.25) * mm, "end": v(-14.5, 14.32) * mm});
            skLineSegment(sketch, "E690", {"start": v(4.18, -3.57) * mm, "end": v(4.36, -3.35) * mm});
            skLineSegment(sketch, "E691", {"start": v(-4.36, 3.35) * mm, "end": v(-4.18, 3.57) * mm});
            skLineSegment(sketch, "E692", {"start": v(13.63, -13.47) * mm, "end": v(13.66, -13.44) * mm});
            skLineSegment(sketch, "E693", {"start": v(-13.66, -10.11) * mm, "end": v(-13.63, -10.08) * mm});
            skLineSegment(sketch, "E694", {"start": v(13.63, 10.08) * mm, "end": v(13.66, 10.11) * mm});
            skLineSegment(sketch, "E695", {"start": v(-13.66, 13.44) * mm, "end": v(-13.63, 13.47) * mm});
            skLineSegment(sketch, "E696", {"start": v(14.56, -14.25) * mm, "end": v(14.62, -14.18) * mm});
            skLineSegment(sketch, "E697", {"start": v(-14.62, 14.18) * mm, "end": v(-14.56, 14.25) * mm});
            skLineSegment(sketch, "E698", {"start": v(-9.92, -13.47) * mm, "end": v(-9.9, -13.44) * mm});
            skLineSegment(sketch, "E699", {"start": v(9.9, -10.11) * mm, "end": v(9.92, -10.08) * mm});
            skLineSegment(sketch, "E700", {"start": v(-9.92, 10.08) * mm, "end": v(-9.9, 10.11) * mm});
            skLineSegment(sketch, "E701", {"start": v(9.9, 13.44) * mm, "end": v(9.92, 13.47) * mm});
            skLineSegment(sketch, "E702", {"start": v(4.36, -3.35) * mm, "end": v(4.53, -3.12) * mm});
            skLineSegment(sketch, "E703", {"start": v(-4.53, 3.12) * mm, "end": v(-4.36, 3.35) * mm});
            skLineSegment(sketch, "E704", {"start": v(14.62, -14.18) * mm, "end": v(14.67, -14.1) * mm});
            skLineSegment(sketch, "E705", {"start": v(-14.67, 14.1) * mm, "end": v(-14.62, 14.18) * mm});
            skLineSegment(sketch, "E706", {"start": v(-9.9, -13.44) * mm, "end": v(-9.87, -13.4) * mm});
            skLineSegment(sketch, "E707", {"start": v(13.66, -13.44) * mm, "end": v(13.68, -13.4) * mm});
            skLineSegment(sketch, "E708", {"start": v(-13.68, -10.15) * mm, "end": v(-13.66, -10.11) * mm});
            skLineSegment(sketch, "E709", {"start": v(9.87, -10.15) * mm, "end": v(9.9, -10.11) * mm});
            skLineSegment(sketch, "E710", {"start": v(13.66, 10.11) * mm, "end": v(13.68, 10.15) * mm});
            skLineSegment(sketch, "E711", {"start": v(-9.9, 10.11) * mm, "end": v(-9.87, 10.15) * mm});
            skLineSegment(sketch, "E712", {"start": v(9.87, 13.4) * mm, "end": v(9.9, 13.44) * mm});
            skLineSegment(sketch, "E713", {"start": v(-13.68, 13.4) * mm, "end": v(-13.66, 13.44) * mm});
            skLineSegment(sketch, "E714", {"start": v(9.84, -10.19) * mm, "end": v(9.87, -10.15) * mm});
            skLineSegment(sketch, "E715", {"start": v(-9.87, 10.15) * mm, "end": v(-9.84, 10.19) * mm});
            skLineSegment(sketch, "E716", {"start": v(-9.87, -13.4) * mm, "end": v(-9.84, -13.36) * mm});
            skLineSegment(sketch, "E717", {"start": v(9.84, 13.36) * mm, "end": v(9.87, 13.4) * mm});
            skLineSegment(sketch, "E718", {"start": v(14.67, -14.1) * mm, "end": v(14.72, -14.03) * mm});
            skLineSegment(sketch, "E719", {"start": v(-14.72, 14.03) * mm, "end": v(-14.67, 14.1) * mm});
            skLineSegment(sketch, "E720", {"start": v(-13.7, -10.19) * mm, "end": v(-13.68, -10.15) * mm});
            skLineSegment(sketch, "E721", {"start": v(13.68, 10.15) * mm, "end": v(13.7, 10.19) * mm});
            skLineSegment(sketch, "E722", {"start": v(13.68, -13.4) * mm, "end": v(13.7, -13.36) * mm});
            skLineSegment(sketch, "E723", {"start": v(-13.7, 13.36) * mm, "end": v(-13.68, 13.4) * mm});
            skLineSegment(sketch, "E724", {"start": v(-6, -0.92) * mm, "end": v(-5.47, 0) * mm});
            skLineSegment(sketch, "E725", {"start": v(5.47, 0) * mm, "end": v(6, 0.92) * mm});
            skLineSegment(sketch, "E726", {"start": v(13.7, -13.36) * mm, "end": v(13.73, -13.32) * mm});
            skLineSegment(sketch, "E727", {"start": v(-13.73, 13.32) * mm, "end": v(-13.7, 13.36) * mm});
            skLineSegment(sketch, "E728", {"start": v(-13.73, -10.23) * mm, "end": v(-13.7, -10.19) * mm});
            skLineSegment(sketch, "E729", {"start": v(13.7, 10.19) * mm, "end": v(13.73, 10.23) * mm});
            skLineSegment(sketch, "E730", {"start": v(14.72, -14.03) * mm, "end": v(14.76, -13.95) * mm});
            skLineSegment(sketch, "E731", {"start": v(-14.76, 13.95) * mm, "end": v(-14.72, 14.03) * mm});
            skLineSegment(sketch, "E732", {"start": v(-9.84, -13.36) * mm, "end": v(-9.82, -13.32) * mm});
            skLineSegment(sketch, "E733", {"start": v(9.82, 13.32) * mm, "end": v(9.84, 13.36) * mm});
            skLineSegment(sketch, "E734", {"start": v(9.82, -10.23) * mm, "end": v(9.84, -10.19) * mm});
            skLineSegment(sketch, "E735", {"start": v(-9.84, 10.19) * mm, "end": v(-9.82, 10.23) * mm});
            skLineSegment(sketch, "E736", {"start": v(-9.82, -13.32) * mm, "end": v(-9.8, -13.28) * mm});
            skLineSegment(sketch, "E737", {"start": v(9.8, -10.27) * mm, "end": v(9.82, -10.23) * mm});
            skLineSegment(sketch, "E738", {"start": v(-9.82, 10.23) * mm, "end": v(-9.8, 10.27) * mm});
            skLineSegment(sketch, "E739", {"start": v(9.8, 13.28) * mm, "end": v(9.82, 13.32) * mm});
            skLineSegment(sketch, "E740", {"start": v(14.76, -13.95) * mm, "end": v(14.8, -13.87) * mm});
            skLineSegment(sketch, "E741", {"start": v(-14.8, 13.87) * mm, "end": v(-14.76, 13.95) * mm});
            skLineSegment(sketch, "E742", {"start": v(13.73, -13.32) * mm, "end": v(13.75, -13.28) * mm});
            skLineSegment(sketch, "E743", {"start": v(-13.75, -10.27) * mm, "end": v(-13.73, -10.23) * mm});
            skLineSegment(sketch, "E744", {"start": v(13.73, 10.23) * mm, "end": v(13.75, 10.27) * mm});
            skLineSegment(sketch, "E745", {"start": v(-13.75, 13.28) * mm, "end": v(-13.73, 13.32) * mm});
            skLineSegment(sketch, "E746", {"start": v(3.27, -1.62) * mm, "end": v(3.35, -1.46) * mm});
            skLineSegment(sketch, "E747", {"start": v(-3.35, 1.46) * mm, "end": v(-3.27, 1.62) * mm});
            skLineSegment(sketch, "E748", {"start": v(14.8, -13.87) * mm, "end": v(14.84, -13.79) * mm});
            skLineSegment(sketch, "E749", {"start": v(-14.84, 13.79) * mm, "end": v(-14.8, 13.87) * mm});
            skLineSegment(sketch, "E750", {"start": v(-9.8, -13.28) * mm, "end": v(-9.78, -13.24) * mm});
            skLineSegment(sketch, "E751", {"start": v(9.78, -10.3) * mm, "end": v(9.8, -10.27) * mm});
            skLineSegment(sketch, "E752", {"start": v(-9.8, 10.27) * mm, "end": v(-9.78, 10.3) * mm});
            skLineSegment(sketch, "E753", {"start": v(9.78, 13.24) * mm, "end": v(9.8, 13.28) * mm});
            skLineSegment(sketch, "E754", {"start": v(13.75, -13.28) * mm, "end": v(13.77, -13.24) * mm});
            skLineSegment(sketch, "E755", {"start": v(-13.77, -10.3) * mm, "end": v(-13.75, -10.27) * mm});
            skLineSegment(sketch, "E756", {"start": v(13.75, 10.27) * mm, "end": v(13.77, 10.3) * mm});
            skLineSegment(sketch, "E757", {"start": v(-13.77, 13.24) * mm, "end": v(-13.75, 13.28) * mm});
            skLineSegment(sketch, "E758", {"start": v(3.35, -1.46) * mm, "end": v(3.41, -1.3) * mm});
            skLineSegment(sketch, "E759", {"start": v(-3.41, 1.3) * mm, "end": v(-3.35, 1.46) * mm});
            skLineSegment(sketch, "E760", {"start": v(13.77, -13.24) * mm, "end": v(13.79, -13.2) * mm});
            skLineSegment(sketch, "E761", {"start": v(-13.79, -10.35) * mm, "end": v(-13.77, -10.3) * mm});
            skLineSegment(sketch, "E762", {"start": v(13.77, 10.3) * mm, "end": v(13.79, 10.35) * mm});
            skLineSegment(sketch, "E763", {"start": v(-13.79, 13.2) * mm, "end": v(-13.77, 13.24) * mm});
            skLineSegment(sketch, "E764", {"start": v(-9.78, -13.24) * mm, "end": v(-9.76, -13.2) * mm});
            skLineSegment(sketch, "E765", {"start": v(9.76, -10.35) * mm, "end": v(9.78, -10.3) * mm});
            skLineSegment(sketch, "E766", {"start": v(-9.78, 10.3) * mm, "end": v(-9.76, 10.35) * mm});
            skLineSegment(sketch, "E767", {"start": v(9.76, 13.2) * mm, "end": v(9.78, 13.24) * mm});
            skLineSegment(sketch, "E768", {"start": v(14.84, -13.79) * mm, "end": v(14.87, -13.7) * mm});
            skLineSegment(sketch, "E769", {"start": v(-14.87, 13.7) * mm, "end": v(-14.84, 13.79) * mm});
            skLineSegment(sketch, "E770", {"start": v(3.41, -1.3) * mm, "end": v(3.47, -1.13) * mm});
            skLineSegment(sketch, "E771", {"start": v(-3.47, 1.13) * mm, "end": v(-3.41, 1.3) * mm});
            skLineSegment(sketch, "E772", {"start": v(-9.76, -13.2) * mm, "end": v(-9.75, -13.16) * mm});
            skLineSegment(sketch, "E773", {"start": v(13.79, -13.2) * mm, "end": v(13.8, -13.16) * mm});
            skLineSegment(sketch, "E774", {"start": v(-13.8, -10.4) * mm, "end": v(-13.79, -10.35) * mm});
            skLineSegment(sketch, "E775", {"start": v(9.75, -10.4) * mm, "end": v(9.76, -10.35) * mm});
            skLineSegment(sketch, "E776", {"start": v(13.79, 10.35) * mm, "end": v(13.8, 10.4) * mm});
            skLineSegment(sketch, "E777", {"start": v(-9.76, 10.35) * mm, "end": v(-9.75, 10.4) * mm});
            skLineSegment(sketch, "E778", {"start": v(9.75, 13.16) * mm, "end": v(9.76, 13.2) * mm});
            skLineSegment(sketch, "E779", {"start": v(-13.8, 13.16) * mm, "end": v(-13.79, 13.2) * mm});
            skLineSegment(sketch, "E780", {"start": v(14.87, -13.7) * mm, "end": v(14.9, -13.62) * mm});
            skLineSegment(sketch, "E781", {"start": v(-14.9, 13.62) * mm, "end": v(-14.87, 13.7) * mm});
            skLineSegment(sketch, "E782", {"start": v(14.9, -13.62) * mm, "end": v(14.93, -13.53) * mm});
            skLineSegment(sketch, "E783", {"start": v(-14.93, 13.53) * mm, "end": v(-14.9, 13.62) * mm});
            skLineSegment(sketch, "E784", {"start": v(-13.81, -10.43) * mm, "end": v(-13.8, -10.4) * mm});
            skLineSegment(sketch, "E785", {"start": v(9.74, -10.43) * mm, "end": v(9.75, -10.4) * mm});
            skLineSegment(sketch, "E786", {"start": v(13.8, 10.4) * mm, "end": v(13.81, 10.43) * mm});
            skLineSegment(sketch, "E787", {"start": v(-9.75, 10.4) * mm, "end": v(-9.74, 10.43) * mm});
            skLineSegment(sketch, "E788", {"start": v(-9.75, -13.16) * mm, "end": v(-9.74, -13.12) * mm});
            skLineSegment(sketch, "E789", {"start": v(13.8, -13.16) * mm, "end": v(13.81, -13.12) * mm});
            skLineSegment(sketch, "E790", {"start": v(9.74, 13.12) * mm, "end": v(9.75, 13.16) * mm});
            skLineSegment(sketch, "E791", {"start": v(-13.81, 13.12) * mm, "end": v(-13.8, 13.16) * mm});
            skLineSegment(sketch, "E792", {"start": v(3.47, -1.13) * mm, "end": v(3.52, -0.96) * mm});
            skLineSegment(sketch, "E793", {"start": v(-3.52, 0.96) * mm, "end": v(-3.47, 1.13) * mm});
            skLineSegment(sketch, "E794", {"start": v(-9.74, -13.12) * mm, "end": v(-9.73, -13.07) * mm});
            skLineSegment(sketch, "E795", {"start": v(13.81, -13.12) * mm, "end": v(13.82, -13.07) * mm});
            skLineSegment(sketch, "E796", {"start": v(9.73, 13.07) * mm, "end": v(9.74, 13.12) * mm});
            skLineSegment(sketch, "E797", {"start": v(-13.82, 13.07) * mm, "end": v(-13.81, 13.12) * mm});
            skLineSegment(sketch, "E798", {"start": v(14.93, -13.53) * mm, "end": v(14.95, -13.45) * mm});
            skLineSegment(sketch, "E799", {"start": v(-13.82, -10.48) * mm, "end": v(-13.81, -10.43) * mm});
            skLineSegment(sketch, "E800", {"start": v(9.73, -10.48) * mm, "end": v(9.74, -10.43) * mm});
            skLineSegment(sketch, "E801", {"start": v(13.81, 10.43) * mm, "end": v(13.82, 10.48) * mm});
            skLineSegment(sketch, "E802", {"start": v(-9.74, 10.43) * mm, "end": v(-9.73, 10.48) * mm});
            skLineSegment(sketch, "E803", {"start": v(-14.95, 13.45) * mm, "end": v(-14.93, 13.53) * mm});
            skLineSegment(sketch, "E804", {"start": v(3.52, -0.96) * mm, "end": v(3.56, -0.79) * mm});
            skLineSegment(sketch, "E805", {"start": v(-3.56, 0.79) * mm, "end": v(-3.52, 0.96) * mm});
            skLineSegment(sketch, "E806", {"start": v(-9.73, -13.07) * mm, "end": v(-9.72, -13.03) * mm});
            skLineSegment(sketch, "E807", {"start": v(13.82, -13.07) * mm, "end": v(13.83, -13.03) * mm});
            skLineSegment(sketch, "E808", {"start": v(-13.83, -10.52) * mm, "end": v(-13.82, -10.48) * mm});
            skLineSegment(sketch, "E809", {"start": v(9.72, -10.52) * mm, "end": v(9.73, -10.48) * mm});
            skLineSegment(sketch, "E810", {"start": v(13.82, 10.48) * mm, "end": v(13.83, 10.52) * mm});
            skLineSegment(sketch, "E811", {"start": v(-9.73, 10.48) * mm, "end": v(-9.72, 10.52) * mm});
            skLineSegment(sketch, "E812", {"start": v(9.72, 13.03) * mm, "end": v(9.73, 13.07) * mm});
            skLineSegment(sketch, "E813", {"start": v(-13.83, 13.03) * mm, "end": v(-13.82, 13.07) * mm});
            skLineSegment(sketch, "E814", {"start": v(14.95, -13.45) * mm, "end": v(14.97, -13.36) * mm});
            skLineSegment(sketch, "E815", {"start": v(-14.97, 13.36) * mm, "end": v(-14.95, 13.45) * mm});
            skLineSegment(sketch, "E816", {"start": v(3.56, -0.79) * mm, "end": v(3.6, -0.61) * mm});
            skLineSegment(sketch, "E817", {"start": v(-3.6, 0.61) * mm, "end": v(-3.56, 0.79) * mm});
            skLineSegment(sketch, "E818", {"start": v(-13.84, -10.57) * mm, "end": v(-13.83, -10.52) * mm});
            skLineSegment(sketch, "E819", {"start": v(9.7, -10.57) * mm, "end": v(9.72, -10.52) * mm});
            skLineSegment(sketch, "E820", {"start": v(13.83, 10.52) * mm, "end": v(13.84, 10.57) * mm});
            skLineSegment(sketch, "E821", {"start": v(-9.72, 10.52) * mm, "end": v(-9.7, 10.57) * mm});
            skLineSegment(sketch, "E822", {"start": v(14.97, -13.36) * mm, "end": v(14.98, -13.27) * mm});
            skLineSegment(sketch, "E823", {"start": v(-14.98, 13.27) * mm, "end": v(-14.97, 13.36) * mm});
            skLineSegment(sketch, "E824", {"start": v(-9.72, -13.03) * mm, "end": v(-9.7, -12.98) * mm});
            skLineSegment(sketch, "E825", {"start": v(13.83, -13.03) * mm, "end": v(13.84, -12.98) * mm});
            skLineSegment(sketch, "E826", {"start": v(9.7, 12.98) * mm, "end": v(9.72, 13.03) * mm});
            skLineSegment(sketch, "E827", {"start": v(-13.84, 12.98) * mm, "end": v(-13.83, 13.03) * mm});
            skLineSegment(sketch, "E828", {"start": v(3.6, -0.61) * mm, "end": v(3.62, -0.44) * mm});
            skLineSegment(sketch, "E829", {"start": v(-3.62, 0.44) * mm, "end": v(-3.6, 0.61) * mm});
            skLineSegment(sketch, "E830", {"start": v(-9.7, -12.98) * mm, "end": v(-9.7, -12.94) * mm});
            skLineSegment(sketch, "E831", {"start": v(9.7, 12.94) * mm, "end": v(9.7, 12.98) * mm});
            skLineSegment(sketch, "E832", {"start": v(9.7, -10.61) * mm, "end": v(9.7, -10.57) * mm});
            skLineSegment(sketch, "E833", {"start": v(-9.7, 10.57) * mm, "end": v(-9.7, 10.61) * mm});
            skLineSegment(sketch, "E834", {"start": v(14.98, -13.27) * mm, "end": v(15, -13.18) * mm});
            skLineSegment(sketch, "E835", {"start": v(-15, 13.18) * mm, "end": v(-14.98, 13.27) * mm});
            skLineSegment(sketch, "E836", {"start": v(13.84, -12.98) * mm, "end": v(13.85, -12.94) * mm});
            skLineSegment(sketch, "E837", {"start": v(-13.85, 12.94) * mm, "end": v(-13.84, 12.98) * mm});
            skLineSegment(sketch, "E838", {"start": v(-13.85, -10.61) * mm, "end": v(-13.84, -10.57) * mm});
            skLineSegment(sketch, "E839", {"start": v(13.84, 10.57) * mm, "end": v(13.85, 10.61) * mm});
            skLineSegment(sketch, "E840", {"start": v(3.62, -0.44) * mm, "end": v(3.64, -0.26) * mm});
            skLineSegment(sketch, "E841", {"start": v(-3.64, 0.26) * mm, "end": v(-3.62, 0.44) * mm});
            skLineSegment(sketch, "E842", {"start": v(13.85, -12.94) * mm, "end": v(13.85, -12.9) * mm});
            skLineSegment(sketch, "E843", {"start": v(-13.85, -10.66) * mm, "end": v(-13.85, -10.61) * mm});
            skLineSegment(sketch, "E844", {"start": v(13.85, 10.61) * mm, "end": v(13.85, 10.66) * mm});
            skLineSegment(sketch, "E845", {"start": v(-13.85, 12.9) * mm, "end": v(-13.85, 12.94) * mm});
            skLineSegment(sketch, "E846", {"start": v(15, -13.18) * mm, "end": v(15, -13.09) * mm});
            skLineSegment(sketch, "E847", {"start": v(-15, 13.09) * mm, "end": v(-15, 13.18) * mm});
            skLineSegment(sketch, "E848", {"start": v(-9.7, -12.94) * mm, "end": v(-9.7, -12.9) * mm});
            skLineSegment(sketch, "E849", {"start": v(9.7, -10.66) * mm, "end": v(9.7, -10.61) * mm});
            skLineSegment(sketch, "E850", {"start": v(-9.7, 10.61) * mm, "end": v(-9.7, 10.66) * mm});
            skLineSegment(sketch, "E851", {"start": v(9.7, 12.9) * mm, "end": v(9.7, 12.94) * mm});
            skLineSegment(sketch, "E852", {"start": v(3.64, -0.26) * mm, "end": v(3.65, -0.09) * mm});
            skLineSegment(sketch, "E853", {"start": v(-3.65, 0.09) * mm, "end": v(-3.64, 0.26) * mm});
            skLineSegment(sketch, "E854", {"start": v(15, -13.09) * mm, "end": v(15, -13) * mm});
            skLineSegment(sketch, "E855", {"start": v(-15, 13) * mm, "end": v(-15, 13.09) * mm});
            skLineSegment(sketch, "E856", {"start": v(-9.7, -12.9) * mm, "end": v(-9.7, -12.85) * mm});
            skLineSegment(sketch, "E857", {"start": v(13.85, -12.9) * mm, "end": v(13.85, -12.85) * mm});
            skLineSegment(sketch, "E858", {"start": v(-13.85, -10.7) * mm, "end": v(-13.85, -10.66) * mm});
            skLineSegment(sketch, "E859", {"start": v(9.7, -10.7) * mm, "end": v(9.7, -10.66) * mm});
            skLineSegment(sketch, "E860", {"start": v(13.85, 10.66) * mm, "end": v(13.85, 10.7) * mm});
            skLineSegment(sketch, "E861", {"start": v(-9.7, 10.66) * mm, "end": v(-9.7, 10.7) * mm});
            skLineSegment(sketch, "E862", {"start": v(9.7, 12.85) * mm, "end": v(9.7, 12.9) * mm});
            skLineSegment(sketch, "E863", {"start": v(-13.85, 12.85) * mm, "end": v(-13.85, 12.9) * mm});
            skLineSegment(sketch, "E864", {"start": v(-12.8, -8.25) * mm, "end": v(-12.8, -4) * mm});
            skLineSegment(sketch, "E865", {"start": v(12.8, 4) * mm, "end": v(12.8, 8.25) * mm});
            skLineSegment(sketch, "E866", {"start": v(-15, 4.5) * mm, "end": v(-15, 13) * mm});
            skLineSegment(sketch, "E867", {"start": v(-15, -13) * mm, "end": v(-15, -4.5) * mm});
            skLineSegment(sketch, "E868", {"start": v(-14.5, 4) * mm, "end": v(-14.5, 4.5) * mm});
            skLineSegment(sketch, "E869", {"start": v(-14.5, -4.5) * mm, "end": v(-14.5, -4) * mm});
            skLineSegment(sketch, "E870", {"start": v(-13.85, -12.85) * mm, "end": v(-13.85, -10.7) * mm});
            skLineSegment(sketch, "E871", {"start": v(-13.85, 10.7) * mm, "end": v(-13.85, 12.85) * mm});
            skLineSegment(sketch, "E872", {"start": v(-9.7, -12.85) * mm, "end": v(-9.7, -10.7) * mm});
            skLineSegment(sketch, "E873", {"start": v(-9.7, 10.7) * mm, "end": v(-9.7, 12.85) * mm});
            skLineSegment(sketch, "E874", {"start": v(-8.25, 10.05) * mm, "end": v(-8.25, 12.8) * mm});
            skLineSegment(sketch, "E875", {"start": v(-8.25, -12.8) * mm, "end": v(-8.25, -10.05) * mm});
            skLineSegment(sketch, "E876", {"start": v(-6, 0.92) * mm, "end": v(-6, 4.2) * mm});
            skLineSegment(sketch, "E877", {"start": v(-6, -4.2) * mm, "end": v(-6, -0.92) * mm});
            skLineSegment(sketch, "E878", {"start": v(-4.5, 14.5) * mm, "end": v(-4.5, 15) * mm});
            skLineSegment(sketch, "E879", {"start": v(-4.5, -15) * mm, "end": v(-4.5, -14.5) * mm});
            skLineSegment(sketch, "E880", {"start": v(-4, 12.8) * mm, "end": v(-4, 14.5) * mm});
            skLineSegment(sketch, "E881", {"start": v(-4, -14.5) * mm, "end": v(-4, -12.8) * mm});
            skLineSegment(sketch, "E882", {"start": v(-3.65, -0.09) * mm, "end": v(-3.65, 0.09) * mm});
            skLineSegment(sketch, "E883", {"start": v(3.65, -0.09) * mm, "end": v(3.65, 0.09) * mm});
            skLineSegment(sketch, "E884", {"start": v(4, 12.8) * mm, "end": v(4, 14.5) * mm});
            skLineSegment(sketch, "E885", {"start": v(4, -14.5) * mm, "end": v(4, -12.8) * mm});
            skLineSegment(sketch, "E886", {"start": v(4.5, 14.5) * mm, "end": v(4.5, 15) * mm});
            skLineSegment(sketch, "E887", {"start": v(4.5, -15) * mm, "end": v(4.5, -14.5) * mm});
            skLineSegment(sketch, "E888", {"start": v(6, 0.92) * mm, "end": v(6, 4.2) * mm});
            skLineSegment(sketch, "E889", {"start": v(6, -4.2) * mm, "end": v(6, -0.92) * mm});
            skLineSegment(sketch, "E890", {"start": v(8.25, 10.05) * mm, "end": v(8.25, 12.8) * mm});
            skLineSegment(sketch, "E891", {"start": v(8.25, -12.8) * mm, "end": v(8.25, -10.05) * mm});
            skLineSegment(sketch, "E892", {"start": v(9.7, -12.85) * mm, "end": v(9.7, -10.7) * mm});
            skLineSegment(sketch, "E893", {"start": v(9.7, 10.7) * mm, "end": v(9.7, 12.85) * mm});
            skLineSegment(sketch, "E894", {"start": v(13.85, -12.85) * mm, "end": v(13.85, -10.7) * mm});
            skLineSegment(sketch, "E895", {"start": v(13.85, 10.7) * mm, "end": v(13.85, 12.85) * mm});
            skLineSegment(sketch, "E896", {"start": v(14.5, 4) * mm, "end": v(14.5, 4.5) * mm});
            skLineSegment(sketch, "E897", {"start": v(14.5, -4.5) * mm, "end": v(14.5, -4) * mm});
            skLineSegment(sketch, "E898", {"start": v(15, 4.5) * mm, "end": v(15, 13) * mm});
            skLineSegment(sketch, "E899", {"start": v(15, -13) * mm, "end": v(15, -4.5) * mm});
            skSolve(sketch);
        }
        {
            var Q0;
            Q0=makeQuery(id+"F0.imprint","IMPRINT",FACE,{"disambiguationData":[TD([[makeQuery(id+"F0.imprint","IMPRINT",EDGE,{"derivedFrom":sQuery(id+"F0.wireOp",EDGE,"E0")}),-1.0]])]});
            extrude(context, id + "F1", {"entities" : qUnion([Q0]), "depth" : 25 * mm});
        }
    });
